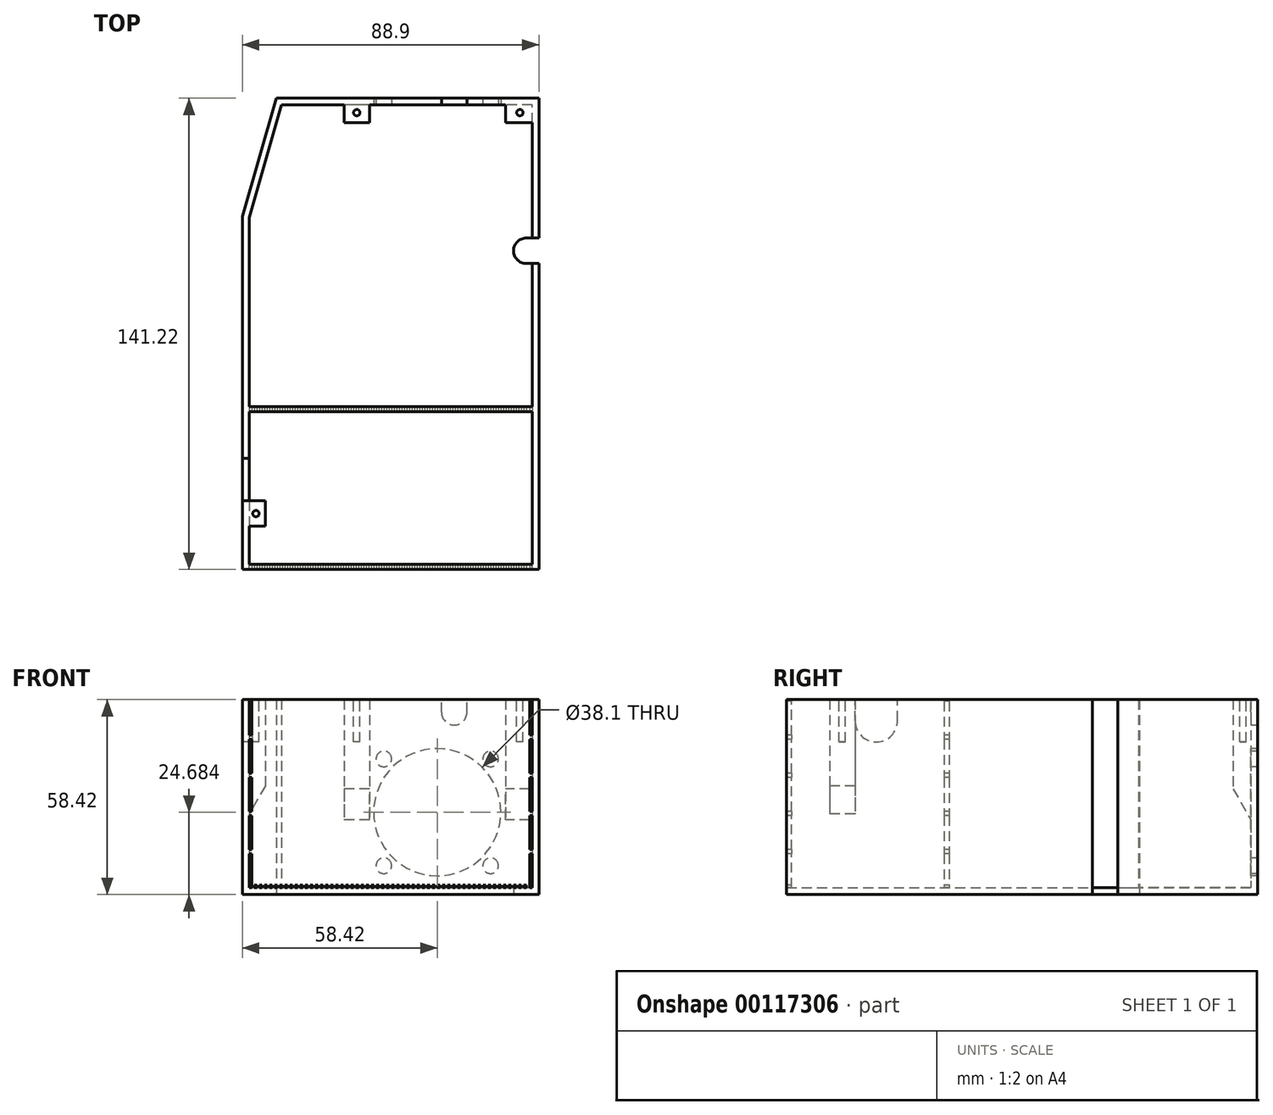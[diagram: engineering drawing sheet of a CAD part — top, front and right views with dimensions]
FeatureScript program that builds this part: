
annotation { "Feature Type Name" : "Feature", "Feature Type Description" : "" }
export const myFeature = defineFeature(function(context is Context, id is Id, definition is map)
    precondition{}
    {
        {
            var Q0;
            Q0=qCreatedBy(makeId("Top.planeOp"),FACE);
            var sketch = newSketch(context, id + "F0", { "sketchPlane" : qUnion([Q0])});
            skLineSegment(sketch, "E0.bottom", {"start": v(44.45, -69.85) * mm, "end": v(-44.45, -69.85) * mm});
            skLineSegment(sketch, "E0.top", {"start": v(44.45, 69.85) * mm, "end": v(-44.45, 69.85) * mm});
            skLineSegment(sketch, "E0.left", {"start": v(44.45, -69.85) * mm, "end": v(44.45, 69.85) * mm});
            skLineSegment(sketch, "E0.right", {"start": v(-44.45, -69.85) * mm, "end": v(-44.45, 69.85) * mm});
            skPoint(sketch, "E0.middle", {"position": v(0, 0) * mm});
            skLineSegment(sketch, "E1", {"start": v(-34.29, 69.85) * mm, "end": v(-44.45, 34.42) * mm});
            skSolve(sketch);
        }
        {
            var Q0;
            Q0=makeQuery(id+"F0.imprint","IMPRINT",FACE,{"disambiguationData":[TD([[makeQuery(id+"F0.imprint","IMPRINT",EDGE,{"derivedFrom":sQuery(id+"F0.wireOp",EDGE,"E0.bottom")}),-1.0]])]});
            extrude(context, id + "F1", {"entities" : qUnion([Q0]), "depth" : 58.42 * mm});
        }
        {
            var Q0;
            Q0=makeQuery(id+"F1.opExtrude","CAP_FACE",FACE,{"disambiguationData":[OSD([sQuery(id+"F0.wireOp",EDGE,"E0.bottom"),sQuery(id+"F0.wireOp",EDGE,"E0.top"),sQuery(id+"F0.wireOp",EDGE,"E0.left"),sQuery(id+"F0.wireOp",EDGE,"E0.right")])],"isStart":false});
            shell(context, id + "F2", {"entities" : qUnion([Q0]), "thickness" : 2.03 * mm});
        }
        {
            var Q0;
            Q0=makeQuery(id+"F2.opShell","OFFSET_FACE",FACE,{"disambiguationData":[OSD([sQuery(id+"F0.wireOp",EDGE,"E0.bottom"),sQuery(id+"F0.wireOp",EDGE,"E0.top"),sQuery(id+"F0.wireOp",EDGE,"E0.left"),sQuery(id+"F0.wireOp",EDGE,"E0.right")])]});
            var sketch = newSketch(context, id + "F3", { "sketchPlane" : qUnion([Q0])});
            skLineSegment(sketch, "E2.bottom", {"start": v(42.42, 67.82) * mm, "end": v(34.42, 67.82) * mm});
            skLineSegment(sketch, "E2.top", {"start": v(42.42, 62.48) * mm, "end": v(34.42, 62.48) * mm});
            skLineSegment(sketch, "E2.left", {"start": v(42.42, 67.82) * mm, "end": v(42.42, 62.48) * mm});
            skLineSegment(sketch, "E2.right", {"start": v(34.42, 67.82) * mm, "end": v(34.42, 62.48) * mm});
            skLineSegment(sketch, "E3.bottom", {"start": v(-13.97, 67.82) * mm, "end": v(-6.35, 67.82) * mm});
            skLineSegment(sketch, "E3.top", {"start": v(-13.97, 62.48) * mm, "end": v(-6.35, 62.48) * mm});
            skLineSegment(sketch, "E3.left", {"start": v(-13.97, 67.82) * mm, "end": v(-13.97, 62.48) * mm});
            skLineSegment(sketch, "E3.right", {"start": v(-6.35, 67.82) * mm, "end": v(-6.35, 62.48) * mm});
            skLineSegment(sketch, "E4.bottom", {"start": v(-42.42, -50.8) * mm, "end": v(-37.6, -50.8) * mm});
            skLineSegment(sketch, "E4.top", {"start": v(-42.42, -58.42) * mm, "end": v(-37.6, -58.42) * mm});
            skLineSegment(sketch, "E4.left", {"start": v(-42.42, -50.8) * mm, "end": v(-42.42, -58.42) * mm});
            skLineSegment(sketch, "E4.right", {"start": v(-37.6, -50.8) * mm, "end": v(-37.6, -58.42) * mm});
            skLineSegment(sketch, "E5.bottom", {"start": v(-42.42, -22.6) * mm, "end": v(42.42, -22.6) * mm});
            skLineSegment(sketch, "E5.top", {"start": v(-42.42, -24.13) * mm, "end": v(42.42, -24.13) * mm});
            skLineSegment(sketch, "E5.left", {"start": v(-42.42, -22.6) * mm, "end": v(-42.42, -24.13) * mm});
            skLineSegment(sketch, "E5.right", {"start": v(42.42, -22.6) * mm, "end": v(42.42, -24.13) * mm});
            skSolve(sketch);
        }
        {
            var Q0;
            Q0 = qSketchRegion(id + "F3", true);
            extrude(context, id + "F4", {"entities" : qUnion([Q0]), "operationType" : NewBodyOperationType.ADD, "depth" : 56.4 * mm});
        }
        {
            var Q0;
            Q0=makeQuery(id+"F4.boolean.opBoolean","MERGE",FACE,{"derivedFrom":[makeQuery(id+"F1.opExtrude","CAP_FACE",FACE,{"disambiguationData":[OSD([sQuery(id+"F0.wireOp",EDGE,"E0.bottom"),sQuery(id+"F0.wireOp",EDGE,"E0.top"),sQuery(id+"F0.wireOp",EDGE,"E0.left"),sQuery(id+"F0.wireOp",EDGE,"E0.right")])],"isStart":false}),makeQuery(id+"F4.opExtrude","CAP_FACE",FACE,{"disambiguationData":[OSD([sQuery(id+"F3.wireOp",EDGE,"E2.bottom"),sQuery(id+"F3.wireOp",EDGE,"E2.top"),sQuery(id+"F3.wireOp",EDGE,"E2.left"),sQuery(id+"F3.wireOp",EDGE,"E2.right")])],"isStart":false}),makeQuery(id+"F4.opExtrude","CAP_FACE",FACE,{"disambiguationData":[OSD([sQuery(id+"F3.wireOp",EDGE,"E3.bottom"),sQuery(id+"F3.wireOp",EDGE,"E3.top"),sQuery(id+"F3.wireOp",EDGE,"E3.left"),sQuery(id+"F3.wireOp",EDGE,"E3.right")])],"isStart":false}),makeQuery(id+"F4.opExtrude","CAP_FACE",FACE,{"disambiguationData":[OSD([sQuery(id+"F3.wireOp",EDGE,"E4.bottom"),sQuery(id+"F3.wireOp",EDGE,"E4.top"),sQuery(id+"F3.wireOp",EDGE,"E4.left"),sQuery(id+"F3.wireOp",EDGE,"E4.right")])],"isStart":false})]});
            var sketch = newSketch(context, id + "F5", { "sketchPlane" : qUnion([Q0])});
            skCircle(sketch, "E6", {"center": v(38.74, 65.53) * mm, "radius": 0.95 * mm});
            skCircle(sketch, "E7", {"center": v(-10.16, 65.53) * mm, "radius": 0.95 * mm});
            skCircle(sketch, "E8", {"center": v(-40.39, -54.6) * mm, "radius": 0.95 * mm});
            skSolve(sketch);
        }
        {
            var Q0;
            Q0 = qSketchRegion(id + "F5", true);
            extrude(context, id + "F6", {"entities" : qUnion([Q0]), "operationType" : NewBodyOperationType.REMOVE, "oppositeDirection" : true, "depth" : 12.7 * mm});
        }
        {
            var Q0;
            Q0=makeQuery(id+"F2.opShell","OFFSET_FACE",FACE,{"disambiguationData":[OSD([sQuery(id+"F0.wireOp",EDGE,"E0.bottom")])]});
            extrude(context, id + "F7", {"entities" : qUnion([Q0]), "operationType" : NewBodyOperationType.REMOVE, "endBound" : BoundingType.UP_TO_NEXT, "oppositeDirection" : true, "depth" : 25.4 * mm});
        }
        {
            var Q0;
            Q0=makeQuery(id+"F1.opExtrude","SWEPT_FACE",FACE,{"disambiguationData":[OSD([sQuery(id+"F0.wireOp",EDGE,"E0.top")])]});
            var sketch = newSketch(context, id + "F8", { "sketchPlane" : qUnion([Q0])});
            skArc(sketch, "E9", {"start": v(-22.86, 54.6) * mm, "mid": v(-19.05, 50.8) * mm, "end": v(-15.24, 54.6) * mm});
            skLineSegment(sketch, "E10", {"start": v(-15.24, 54.6) * mm, "end": v(-15.24, 58.42) * mm});
            skLineSegment(sketch, "E11", {"start": v(-22.86, 54.6) * mm, "end": v(-22.86, 58.42) * mm});
            skLineSegment(sketch, "E12", {"start": v(-15.24, 58.42) * mm, "end": v(-22.86, 58.42) * mm});
            skSolve(sketch);
        }
        {
            var Q0;
            Q0 = qSketchRegion(id + "F8", true);
            extrude(context, id + "F9", {"entities" : qUnion([Q0]), "operationType" : NewBodyOperationType.REMOVE, "endBound" : BoundingType.UP_TO_NEXT, "oppositeDirection" : true, "depth" : 25.4 * mm});
        }
        {
            var Q0;
            Q0=makeQuery(id+"F1.opExtrude","SWEPT_FACE",FACE,{"disambiguationData":[OSD([sQuery(id+"F0.wireOp",EDGE,"E0.left")])]});
            var sketch = newSketch(context, id + "F10", { "sketchPlane" : qUnion([Q0])});
            skLineSegment(sketch, "E13", {"start": v(27.94, 6.35) * mm, "end": v(27.94, 58.42) * mm});
            skLineSegment(sketch, "E14", {"start": v(20.32, 6.35) * mm, "end": v(20.32, 58.42) * mm});
            skLineSegment(sketch, "E15", {"start": v(20.32, 58.42) * mm, "end": v(27.94, 58.42) * mm});
            skLineSegment(sketch, "E16", {"start": v(20.32, 6.35) * mm, "end": v(20.32, 2.54) * mm});
            skLineSegment(sketch, "E17", {"start": v(20.32, 2.54) * mm, "end": v(27.94, 2.54) * mm});
            skLineSegment(sketch, "E18", {"start": v(27.94, 2.54) * mm, "end": v(27.94, 6.35) * mm});
            skSolve(sketch);
        }
        {
            var Q0;
            Q0 = qSketchRegion(id + "F10", true);
            extrude(context, id + "F11", {"entities" : qUnion([Q0]), "operationType" : NewBodyOperationType.REMOVE, "endBound" : BoundingType.UP_TO_NEXT, "oppositeDirection" : true, "depth" : 25.4 * mm});
        }
        {
            var Q0;
            Q0=makeQuery(id+"F1.opExtrude","SWEPT_FACE",FACE,{"disambiguationData":[OSD([sQuery(id+"F0.wireOp",EDGE,"E0.right")])]});
            var sketch = newSketch(context, id + "F12", { "sketchPlane" : qUnion([Q0])});
            skArc(sketch, "E19", {"start": v(38.1, 52.07) * mm, "mid": v(44.45, 45.72) * mm, "end": v(50.8, 52.07) * mm});
            skLineSegment(sketch, "E20", {"start": v(50.8, 52.07) * mm, "end": v(50.8, 58.42) * mm});
            skLineSegment(sketch, "E21", {"start": v(38.1, 52.07) * mm, "end": v(38.1, 58.42) * mm});
            skLineSegment(sketch, "E22", {"start": v(38.1, 58.42) * mm, "end": v(50.8, 58.42) * mm});
            skSolve(sketch);
        }
        {
            var Q0;
            Q0 = qSketchRegion(id + "F12", true);
            extrude(context, id + "F13", {"entities" : qUnion([Q0]), "operationType" : NewBodyOperationType.REMOVE, "endBound" : BoundingType.UP_TO_NEXT, "oppositeDirection" : true, "depth" : 25.4 * mm});
        }
        {
            var Q0;
            Q0=makeQuery(id+"F1.opExtrude","CAP_FACE",FACE,{"disambiguationData":[OSD([sQuery(id+"F0.wireOp",EDGE,"E0.bottom"),sQuery(id+"F0.wireOp",EDGE,"E0.top"),sQuery(id+"F0.wireOp",EDGE,"E0.left"),sQuery(id+"F0.wireOp",EDGE,"E0.right")])],"isStart":true});
            var sketch = newSketch(context, id + "F14", { "sketchPlane" : qUnion([Q0])});
            skLineSegment(sketch, "E23", {"start": v(-34.29, -69.85) * mm, "end": v(-44.45, -34.42) * mm});
            skSolve(sketch);
        }
        {
            var Q0;
            Q0=makeQuery(id+"F4.opExtrude","SWEPT_FACE",FACE,{"disambiguationData":[OSD([sQuery(id+"F3.wireOp",EDGE,"E4.top")])]});
            var sketch = newSketch(context, id + "F15", { "sketchPlane" : qUnion([Q0])});
            skLineSegment(sketch, "E24", {"start": v(-37.6, 32.58) * mm, "end": v(-42.42, 24.22) * mm});
            skLineSegment(sketch, "E25", {"start": v(-42.42, 24.22) * mm, "end": v(-42.42, 2.03) * mm});
            skLineSegment(sketch, "E26", {"start": v(-42.42, 2.03) * mm, "end": v(-37.6, 2.03) * mm});
            skLineSegment(sketch, "E27", {"start": v(-37.6, 2.03) * mm, "end": v(-37.6, 32.58) * mm});
            skSolve(sketch);
        }
        {
            var Q0;
            Q0 = qSketchRegion(id + "F15", true);
            extrude(context, id + "F16", {"entities" : qUnion([Q0]), "operationType" : NewBodyOperationType.REMOVE, "endBound" : BoundingType.UP_TO_NEXT, "oppositeDirection" : true, "depth" : 25.4 * mm});
        }
        {
            var Q0;
            Q0=makeQuery(id+"F4.opExtrude","SWEPT_FACE",FACE,{"disambiguationData":[OSD([sQuery(id+"F3.wireOp",EDGE,"E3.left")])]});
            var sketch = newSketch(context, id + "F17", { "sketchPlane" : qUnion([Q0])});
            skLineSegment(sketch, "E28", {"start": v(-62.48, 31.7) * mm, "end": v(-67.82, 22.46) * mm});
            skSolve(sketch);
        }
        {
            var Q0;
            {var subQ0=sQuery(id+"F17.wireOp",EDGE,"E28");Q0=makeQuery(id+"F17.imprint","IMPRINT",FACE,{"disambiguationData":[TD([[makeQuery(id+"F17.imprint","IMPRINT",EDGE,{"derivedFrom":subQ0}),1.0]])]});}
            extrude(context, id + "F18", {"entities" : qUnion([Q0]), "operationType" : NewBodyOperationType.REMOVE, "oppositeDirection" : true, "depth" : 56.4 * mm});
        }
        {
            var Q0;
            {var subQ0=sQuery(id+"F3.wireOp",EDGE,"E3.left");var subQ1=sQuery(id+"F3.wireOp",EDGE,"E3.bottom");var subQ2=sQuery(id+"F0.wireOp",EDGE,"E0.top");var subQ3=sQuery(id+"F3.wireOp",EDGE,"E2.right");var subQ6=sQuery(id+"F0.wireOp",EDGE,"E1");var subQ14=makeQuery(id+"F2.opShell","OFFSET_FACE",FACE,{"disambiguationData":[OSD([subQ2])]});Q0=makeQuery(id+"F18.boolean.opBoolean","MERGE",FACE,{"derivedFrom":[makeQuery(id+"F4.boolean.opBoolean","SPLIT",FACE,{"disambiguationData":[TD([makeQuery(id+"F2.opShell","OFFSET_FACE",FACE,{"disambiguationData":[OSD([subQ6])]})])],"derivedFrom":subQ14}),makeQuery(id+"F4.boolean.opBoolean","SPLIT",FACE,{"disambiguationData":[TD([makeQuery(id+"F4.opExtrude","SWEPT_FACE",FACE,{"disambiguationData":[OSD([subQ3])]})])],"derivedFrom":subQ14}),makeQuery(id+"F18.opExtrude","SWEPT_FACE",FACE,{"disambiguationData":[OSD([subQ2,subQ1,subQ0])]})]});}
            var sketch = newSketch(context, id + "F19", { "sketchPlane" : qUnion([Q0])});
            skCircle(sketch, "E29", {"center": v(-2.03, 8.64) * mm, "radius": 2.35 * mm});
            skCircle(sketch, "E30", {"center": v(29.97, 8.64) * mm, "radius": 2.35 * mm});
            skCircle(sketch, "E31", {"center": v(-2.03, 40.64) * mm, "radius": 2.35 * mm});
            skCircle(sketch, "E32", {"center": v(29.97, 40.64) * mm, "radius": 2.35 * mm});
            skCircle(sketch, "E33", {"center": v(13.97, 24.68) * mm, "radius": 19.05 * mm});
            skSolve(sketch);
        }
        {
            var Q0;
            Q0 = qSketchRegion(id + "F19", true);
            extrude(context, id + "F20", {"entities" : qUnion([Q0]), "operationType" : NewBodyOperationType.REMOVE, "endBound" : BoundingType.UP_TO_NEXT, "oppositeDirection" : true, "depth" : 25.4 * mm});
        }
        {
            var Q0;
            Q0=makeQuery(id+"F14.imprint","IMPRINT",FACE,{"disambiguationData":[TD([[makeQuery(id+"F14.imprint","IMPRINT",EDGE,{"derivedFrom":sQuery(id+"F14.wireOp",EDGE,"E23")}),-1.0]])]});
            var sketch = newSketch(context, id + "F21", { "sketchPlane" : qUnion([Q0])});
            skCircle(sketch, "E34", {"center": v(-8.9, -19.05) * mm, "radius": 19.05 * mm});
            skCircle(sketch, "E35", {"center": v(6.99, -35) * mm, "radius": 2.35 * mm});
            skCircle(sketch, "E36", {"center": v(-25.02, -35) * mm, "radius": 2.35 * mm});
            skCircle(sketch, "E37", {"center": v(-25.02, -3) * mm, "radius": 2.35 * mm});
            skCircle(sketch, "E38", {"center": v(6.99, -3) * mm, "radius": 2.35 * mm});
            skCircle(sketch, "E39", {"center": v(-25.02, -35) * mm, "radius": 1.52 * mm});
            skCircle(sketch, "E40", {"center": v(6.99, -35) * mm, "radius": 1.52 * mm});
            skCircle(sketch, "E41", {"center": v(6.99, -3) * mm, "radius": 1.52 * mm});
            skCircle(sketch, "E42", {"center": v(-25.02, -3) * mm, "radius": 1.52 * mm});
            skCircle(sketch, "E43", {"center": v(-8.9, -19.05) * mm, "radius": 17.78 * mm});
            skLineSegment(sketch, "E44", {"start": v(-8.9, -44.54) * mm, "end": v(-8.9, 4.8) * mm, "construction": true});
            skLineSegment(sketch, "E45", {"start": v(-33.52, -19.05) * mm, "end": v(14.85, -19.05) * mm, "construction": true});
            skLineSegment(sketch, "E46", {"start": v(-9.98, -36.8) * mm, "end": v(-10.05, -38.06) * mm});
            skLineSegment(sketch, "E47.MirrorCS", {"start": v(-7.8, -36.8) * mm, "end": v(-7.73, -38.06) * mm});
            skLineSegment(sketch, "E48", {"start": v(8.86, -20.14) * mm, "end": v(10.12, -20.21) * mm});
            skLineSegment(sketch, "E49.MirrorCS", {"start": v(8.86, -17.96) * mm, "end": v(10.12, -17.89) * mm});
            skLineSegment(sketch, "E50", {"start": v(-8.2, -1.28) * mm, "end": v(-8.11, -0.02) * mm});
            skLineSegment(sketch, "E51", {"start": v(-26.64, -17.95) * mm, "end": v(-27.9, -17.87) * mm});
            skLineSegment(sketch, "E52.MirrorCS", {"start": v(-9.59, -1.28) * mm, "end": v(-9.67, -0.02) * mm});
            skLineSegment(sketch, "E53", {"start": v(-27.9, -20.23) * mm, "end": v(-26.64, -20.15) * mm});
            skSolve(sketch);
        }
        {
            var Q0;
            Q0=makeQuery(id+"F1.opExtrude","CAP_FACE",FACE,{"disambiguationData":[OSD([sQuery(id+"F0.wireOp",EDGE,"E0.bottom"),sQuery(id+"F0.wireOp",EDGE,"E0.top"),sQuery(id+"F0.wireOp",EDGE,"E0.left"),sQuery(id+"F0.wireOp",EDGE,"E0.right"),sQuery(id+"F0.wireOp",EDGE,"E1")])],"isStart":true});
            var sketch = newSketch(context, id + "F22", { "sketchPlane" : qUnion([Q0])});
            skLineSegment(sketch, "E54", {"start": v(44.45, -27.94) * mm, "end": v(40.64, -27.94) * mm});
            skLineSegment(sketch, "E55", {"start": v(44.45, -20.32) * mm, "end": v(40.64, -20.32) * mm});
            skArc(sketch, "E56", {"start": v(40.64, -27.94) * mm, "mid": v(36.83, -24.13) * mm, "end": v(40.64, -20.32) * mm});
            skLineSegment(sketch, "E57", {"start": v(44.45, -20.32) * mm, "end": v(44.45, -27.94) * mm});
            skSolve(sketch);
        }
        {
            var Q0;
            Q0 = qSketchRegion(id + "F22", true);
            extrude(context, id + "F23", {"entities" : qUnion([Q0]), "operationType" : NewBodyOperationType.REMOVE, "endBound" : BoundingType.UP_TO_NEXT, "oppositeDirection" : true, "depth" : 25.4 * mm});
        }
        {
            var Q0;
            Q0=makeQuery(id+"F1.opExtrude","SWEPT_FACE",FACE,{"disambiguationData":[OSD([sQuery(id+"F0.wireOp",EDGE,"E0.bottom")])]});
            var sketch = newSketch(context, id + "F24", { "sketchPlane" : qUnion([Q0])});
            skLineSegment(sketch, "E58.bottom", {"start": v(-44.45, 58.42) * mm, "end": v(44.45, 58.42) * mm});
            skLineSegment(sketch, "E58.top", {"start": v(-44.45, 0) * mm, "end": v(44.45, 0) * mm});
            skLineSegment(sketch, "E58.left", {"start": v(-44.45, 58.42) * mm, "end": v(-44.45, 0) * mm});
            skLineSegment(sketch, "E58.right", {"start": v(44.45, 58.42) * mm, "end": v(44.45, 0) * mm});
            skSolve(sketch);
        }
        {
            var Q0;
            Q0 = qSketchRegion(id + "F24", true);
            extrude(context, id + "F25", {"entities" : qUnion([Q0]), "operationType" : NewBodyOperationType.ADD, "depth" : 1.52 * mm});
        }
        {
            var Q0;
            Q0=makeQuery(id+"F25.opExtrude","CAP_FACE",FACE,{"disambiguationData":[OSD([sQuery(id+"F24.wireOp",EDGE,"E58.bottom"),sQuery(id+"F24.wireOp",EDGE,"E58.top"),sQuery(id+"F24.wireOp",EDGE,"E58.left"),sQuery(id+"F24.wireOp",EDGE,"E58.right")])],"isStart":false});
            var sketch = newSketch(context, id + "F26", { "sketchPlane" : qUnion([Q0])});
            skLineSegment(sketch, "E59.bottom", {"start": v(-42.42, 12.2) * mm, "end": v(-41.66, 12.2) * mm});
            skLineSegment(sketch, "E59.top", {"start": v(-42.42, 2.03) * mm, "end": v(-41.66, 2.03) * mm});
            skLineSegment(sketch, "E59.left", {"start": v(-42.42, 12.2) * mm, "end": v(-42.42, 2.03) * mm});
            skLineSegment(sketch, "E59.right", {"start": v(-41.66, 12.2) * mm, "end": v(-41.66, 2.03) * mm});
            skLineSegment(sketch, "E60.0.1.0", {"start": v(-42.42, 23.62) * mm, "end": v(-42.42, 13.46) * mm});
            skLineSegment(sketch, "E60.0.1.1", {"start": v(-41.66, 23.62) * mm, "end": v(-41.66, 13.46) * mm});
            skLineSegment(sketch, "E60.0.1.2", {"start": v(-42.42, 23.62) * mm, "end": v(-41.66, 23.62) * mm});
            skLineSegment(sketch, "E60.0.1.3", {"start": v(-42.42, 13.46) * mm, "end": v(-41.66, 13.46) * mm});
            skLineSegment(sketch, "E60.0.2.0", {"start": v(-42.42, 35.05) * mm, "end": v(-42.42, 24.9) * mm});
            skLineSegment(sketch, "E60.0.2.1", {"start": v(-41.66, 35.05) * mm, "end": v(-41.66, 24.9) * mm});
            skLineSegment(sketch, "E60.0.2.2", {"start": v(-42.42, 35.05) * mm, "end": v(-41.66, 35.05) * mm});
            skLineSegment(sketch, "E60.0.2.3", {"start": v(-42.42, 24.9) * mm, "end": v(-41.66, 24.9) * mm});
            skLineSegment(sketch, "E60.0.3.0", {"start": v(-42.42, 46.48) * mm, "end": v(-42.42, 36.32) * mm});
            skLineSegment(sketch, "E60.0.3.1", {"start": v(-41.66, 46.48) * mm, "end": v(-41.66, 36.32) * mm});
            skLineSegment(sketch, "E60.0.3.2", {"start": v(-42.42, 46.48) * mm, "end": v(-41.66, 46.48) * mm});
            skLineSegment(sketch, "E60.0.3.3", {"start": v(-42.42, 36.32) * mm, "end": v(-41.66, 36.32) * mm});
            skLineSegment(sketch, "E60.0.4.0", {"start": v(-42.42, 57.91) * mm, "end": v(-42.42, 47.75) * mm});
            skLineSegment(sketch, "E60.0.4.1", {"start": v(-41.66, 57.91) * mm, "end": v(-41.66, 47.75) * mm});
            skLineSegment(sketch, "E60.0.4.2", {"start": v(-42.42, 57.91) * mm, "end": v(-41.66, 57.91) * mm});
            skLineSegment(sketch, "E60.0.4.3", {"start": v(-42.42, 47.75) * mm, "end": v(-41.66, 47.75) * mm});
            skLineSegment(sketch, "E60.direction1", {"start": v(-42.42, 2.03) * mm, "end": v(-36.73, 2.03) * mm, "construction": true});
            skLineSegment(sketch, "E60.direction2", {"start": v(-42.42, 2.03) * mm, "end": v(-42.42, 13.46) * mm, "construction": true});
            skLineSegment(sketch, "E61.1.0.0", {"start": v(42.42, 35.05) * mm, "end": v(42.42, 24.9) * mm});
            skLineSegment(sketch, "E61.1.0.1", {"start": v(41.66, 35.05) * mm, "end": v(41.66, 24.9) * mm});
            skLineSegment(sketch, "E61.1.0.3", {"start": v(41.66, 57.91) * mm, "end": v(41.66, 47.75) * mm});
            skLineSegment(sketch, "E61.1.0.12", {"start": v(41.66, 23.62) * mm, "end": v(41.66, 13.46) * mm});
            skLineSegment(sketch, "E61.1.0.19", {"start": v(42.42, 12.2) * mm, "end": v(42.42, 2.03) * mm});
            skLineSegment(sketch, "E61.1.0.20", {"start": v(41.66, 46.48) * mm, "end": v(41.66, 36.32) * mm});
            skLineSegment(sketch, "E61.1.0.21", {"start": v(42.42, 46.48) * mm, "end": v(42.42, 36.32) * mm});
            skLineSegment(sketch, "E61.1.0.22", {"start": v(41.66, 2.03) * mm, "end": v(41.66, 13.46) * mm, "construction": true});
            skLineSegment(sketch, "E61.1.0.26", {"start": v(41.66, 2.03) * mm, "end": v(47.34, 2.03) * mm, "construction": true});
            skLineSegment(sketch, "E61.1.0.29", {"start": v(42.42, 57.91) * mm, "end": v(42.42, 47.75) * mm});
            skLineSegment(sketch, "E61.1.0.30", {"start": v(42.42, 23.62) * mm, "end": v(42.42, 13.46) * mm});
            skLineSegment(sketch, "E61.1.0.31", {"start": v(41.66, 12.2) * mm, "end": v(41.66, 2.03) * mm});
            skLineSegment(sketch, "E61.1.0.32", {"start": v(41.66, 13.46) * mm, "end": v(42.42, 13.46) * mm});
            skLineSegment(sketch, "E61.1.0.33", {"start": v(41.66, 23.62) * mm, "end": v(42.42, 23.62) * mm});
            skLineSegment(sketch, "E61.1.0.50", {"start": v(41.66, 57.91) * mm, "end": v(42.42, 57.91) * mm});
            skLineSegment(sketch, "E61.1.0.53", {"start": v(41.66, 2.03) * mm, "end": v(42.42, 2.03) * mm});
            skLineSegment(sketch, "E61.1.0.54", {"start": v(41.66, 12.2) * mm, "end": v(42.42, 12.2) * mm});
            skLineSegment(sketch, "E61.1.0.55", {"start": v(41.66, 36.32) * mm, "end": v(42.42, 36.32) * mm});
            skLineSegment(sketch, "E61.1.0.56", {"start": v(41.66, 47.75) * mm, "end": v(42.42, 47.75) * mm});
            skLineSegment(sketch, "E61.1.0.59", {"start": v(41.66, 24.9) * mm, "end": v(42.42, 24.9) * mm});
            skLineSegment(sketch, "E61.1.0.60", {"start": v(41.66, 35.05) * mm, "end": v(42.42, 35.05) * mm});
            skLineSegment(sketch, "E61.1.0.61", {"start": v(41.66, 46.48) * mm, "end": v(42.42, 46.48) * mm});
            skLineSegment(sketch, "E61.direction1", {"start": v(-42.42, 2.03) * mm, "end": v(41.66, 2.03) * mm, "construction": true});
            skLineSegment(sketch, "E62.bottom", {"start": v(-40.9, 2.8) * mm, "end": v(-40.13, 2.8) * mm});
            skLineSegment(sketch, "E62.top", {"start": v(-40.9, 2.03) * mm, "end": v(-40.13, 2.03) * mm});
            skLineSegment(sketch, "E62.left", {"start": v(-40.9, 2.8) * mm, "end": v(-40.9, 2.03) * mm});
            skLineSegment(sketch, "E62.right", {"start": v(-40.13, 2.8) * mm, "end": v(-40.13, 2.03) * mm});
            skLineSegment(sketch, "E63.1.0.0", {"start": v(-39.37, 2.8) * mm, "end": v(-38.6, 2.8) * mm});
            skLineSegment(sketch, "E63.1.0.1", {"start": v(-38.6, 2.8) * mm, "end": v(-38.6, 2.03) * mm});
            skLineSegment(sketch, "E63.1.0.2", {"start": v(-39.37, 2.8) * mm, "end": v(-39.37, 2.03) * mm});
            skLineSegment(sketch, "E63.1.0.3", {"start": v(-39.37, 2.03) * mm, "end": v(-38.6, 2.03) * mm});
            skLineSegment(sketch, "E63.2.0.0", {"start": v(-37.85, 2.8) * mm, "end": v(-37.08, 2.8) * mm});
            skLineSegment(sketch, "E63.2.0.1", {"start": v(-37.08, 2.8) * mm, "end": v(-37.08, 2.03) * mm});
            skLineSegment(sketch, "E63.2.0.2", {"start": v(-37.85, 2.8) * mm, "end": v(-37.85, 2.03) * mm});
            skLineSegment(sketch, "E63.2.0.3", {"start": v(-37.85, 2.03) * mm, "end": v(-37.08, 2.03) * mm});
            skLineSegment(sketch, "E63.3.0.0", {"start": v(-36.32, 2.8) * mm, "end": v(-35.56, 2.8) * mm});
            skLineSegment(sketch, "E63.3.0.1", {"start": v(-35.56, 2.8) * mm, "end": v(-35.56, 2.03) * mm});
            skLineSegment(sketch, "E63.3.0.2", {"start": v(-36.32, 2.8) * mm, "end": v(-36.32, 2.03) * mm});
            skLineSegment(sketch, "E63.3.0.3", {"start": v(-36.32, 2.03) * mm, "end": v(-35.56, 2.03) * mm});
            skLineSegment(sketch, "E63.4.0.0", {"start": v(-34.8, 2.8) * mm, "end": v(-34.04, 2.8) * mm});
            skLineSegment(sketch, "E63.4.0.1", {"start": v(-34.04, 2.8) * mm, "end": v(-34.04, 2.03) * mm});
            skLineSegment(sketch, "E63.4.0.2", {"start": v(-34.8, 2.8) * mm, "end": v(-34.8, 2.03) * mm});
            skLineSegment(sketch, "E63.4.0.3", {"start": v(-34.8, 2.03) * mm, "end": v(-34.04, 2.03) * mm});
            skLineSegment(sketch, "E63.5.0.0", {"start": v(-33.27, 2.8) * mm, "end": v(-32.51, 2.8) * mm});
            skLineSegment(sketch, "E63.5.0.1", {"start": v(-32.51, 2.8) * mm, "end": v(-32.51, 2.03) * mm});
            skLineSegment(sketch, "E63.5.0.2", {"start": v(-33.27, 2.8) * mm, "end": v(-33.27, 2.03) * mm});
            skLineSegment(sketch, "E63.5.0.3", {"start": v(-33.27, 2.03) * mm, "end": v(-32.51, 2.03) * mm});
            skLineSegment(sketch, "E63.6.0.0", {"start": v(-31.75, 2.8) * mm, "end": v(-30.99, 2.8) * mm});
            skLineSegment(sketch, "E63.6.0.1", {"start": v(-30.99, 2.8) * mm, "end": v(-30.99, 2.03) * mm});
            skLineSegment(sketch, "E63.6.0.2", {"start": v(-31.75, 2.8) * mm, "end": v(-31.75, 2.03) * mm});
            skLineSegment(sketch, "E63.6.0.3", {"start": v(-31.75, 2.03) * mm, "end": v(-30.99, 2.03) * mm});
            skLineSegment(sketch, "E63.7.0.0", {"start": v(-30.23, 2.8) * mm, "end": v(-29.46, 2.8) * mm});
            skLineSegment(sketch, "E63.7.0.1", {"start": v(-29.46, 2.8) * mm, "end": v(-29.46, 2.03) * mm});
            skLineSegment(sketch, "E63.7.0.2", {"start": v(-30.23, 2.8) * mm, "end": v(-30.23, 2.03) * mm});
            skLineSegment(sketch, "E63.7.0.3", {"start": v(-30.23, 2.03) * mm, "end": v(-29.46, 2.03) * mm});
            skLineSegment(sketch, "E63.8.0.0", {"start": v(-28.7, 2.8) * mm, "end": v(-27.94, 2.8) * mm});
            skLineSegment(sketch, "E63.8.0.1", {"start": v(-27.94, 2.8) * mm, "end": v(-27.94, 2.03) * mm});
            skLineSegment(sketch, "E63.8.0.2", {"start": v(-28.7, 2.8) * mm, "end": v(-28.7, 2.03) * mm});
            skLineSegment(sketch, "E63.8.0.3", {"start": v(-28.7, 2.03) * mm, "end": v(-27.94, 2.03) * mm});
            skLineSegment(sketch, "E63.9.0.0", {"start": v(-27.18, 2.8) * mm, "end": v(-26.42, 2.8) * mm});
            skLineSegment(sketch, "E63.9.0.1", {"start": v(-26.42, 2.8) * mm, "end": v(-26.42, 2.03) * mm});
            skLineSegment(sketch, "E63.9.0.2", {"start": v(-27.18, 2.8) * mm, "end": v(-27.18, 2.03) * mm});
            skLineSegment(sketch, "E63.9.0.3", {"start": v(-27.18, 2.03) * mm, "end": v(-26.42, 2.03) * mm});
            skLineSegment(sketch, "E63.10.0.0", {"start": v(-25.65, 2.8) * mm, "end": v(-24.9, 2.8) * mm});
            skLineSegment(sketch, "E63.10.0.1", {"start": v(-24.9, 2.8) * mm, "end": v(-24.9, 2.03) * mm});
            skLineSegment(sketch, "E63.10.0.2", {"start": v(-25.65, 2.8) * mm, "end": v(-25.65, 2.03) * mm});
            skLineSegment(sketch, "E63.10.0.3", {"start": v(-25.65, 2.03) * mm, "end": v(-24.9, 2.03) * mm});
            skLineSegment(sketch, "E63.11.0.0", {"start": v(-24.13, 2.8) * mm, "end": v(-23.37, 2.8) * mm});
            skLineSegment(sketch, "E63.11.0.1", {"start": v(-23.37, 2.8) * mm, "end": v(-23.37, 2.03) * mm});
            skLineSegment(sketch, "E63.11.0.2", {"start": v(-24.13, 2.8) * mm, "end": v(-24.13, 2.03) * mm});
            skLineSegment(sketch, "E63.11.0.3", {"start": v(-24.13, 2.03) * mm, "end": v(-23.37, 2.03) * mm});
            skLineSegment(sketch, "E63.12.0.0", {"start": v(-22.6, 2.8) * mm, "end": v(-21.84, 2.8) * mm});
            skLineSegment(sketch, "E63.12.0.1", {"start": v(-21.84, 2.8) * mm, "end": v(-21.84, 2.03) * mm});
            skLineSegment(sketch, "E63.12.0.2", {"start": v(-22.6, 2.8) * mm, "end": v(-22.6, 2.03) * mm});
            skLineSegment(sketch, "E63.12.0.3", {"start": v(-22.6, 2.03) * mm, "end": v(-21.84, 2.03) * mm});
            skLineSegment(sketch, "E63.13.0.0", {"start": v(-21.08, 2.8) * mm, "end": v(-20.32, 2.8) * mm});
            skLineSegment(sketch, "E63.13.0.1", {"start": v(-20.32, 2.8) * mm, "end": v(-20.32, 2.03) * mm});
            skLineSegment(sketch, "E63.13.0.2", {"start": v(-21.08, 2.8) * mm, "end": v(-21.08, 2.03) * mm});
            skLineSegment(sketch, "E63.13.0.3", {"start": v(-21.08, 2.03) * mm, "end": v(-20.32, 2.03) * mm});
            skLineSegment(sketch, "E63.14.0.0", {"start": v(-19.56, 2.8) * mm, "end": v(-18.8, 2.8) * mm});
            skLineSegment(sketch, "E63.14.0.1", {"start": v(-18.8, 2.8) * mm, "end": v(-18.8, 2.03) * mm});
            skLineSegment(sketch, "E63.14.0.2", {"start": v(-19.56, 2.8) * mm, "end": v(-19.56, 2.03) * mm});
            skLineSegment(sketch, "E63.14.0.3", {"start": v(-19.56, 2.03) * mm, "end": v(-18.8, 2.03) * mm});
            skLineSegment(sketch, "E63.15.0.0", {"start": v(-18.03, 2.8) * mm, "end": v(-17.27, 2.8) * mm});
            skLineSegment(sketch, "E63.15.0.1", {"start": v(-17.27, 2.8) * mm, "end": v(-17.27, 2.03) * mm});
            skLineSegment(sketch, "E63.15.0.2", {"start": v(-18.03, 2.8) * mm, "end": v(-18.03, 2.03) * mm});
            skLineSegment(sketch, "E63.15.0.3", {"start": v(-18.03, 2.03) * mm, "end": v(-17.27, 2.03) * mm});
            skLineSegment(sketch, "E63.16.0.0", {"start": v(-16.51, 2.8) * mm, "end": v(-15.75, 2.8) * mm});
            skLineSegment(sketch, "E63.16.0.1", {"start": v(-15.75, 2.8) * mm, "end": v(-15.75, 2.03) * mm});
            skLineSegment(sketch, "E63.16.0.2", {"start": v(-16.51, 2.8) * mm, "end": v(-16.51, 2.03) * mm});
            skLineSegment(sketch, "E63.16.0.3", {"start": v(-16.51, 2.03) * mm, "end": v(-15.75, 2.03) * mm});
            skLineSegment(sketch, "E63.17.0.0", {"start": v(-14.99, 2.8) * mm, "end": v(-14.22, 2.8) * mm});
            skLineSegment(sketch, "E63.17.0.1", {"start": v(-14.22, 2.8) * mm, "end": v(-14.22, 2.03) * mm});
            skLineSegment(sketch, "E63.17.0.2", {"start": v(-14.99, 2.8) * mm, "end": v(-14.99, 2.03) * mm});
            skLineSegment(sketch, "E63.17.0.3", {"start": v(-14.99, 2.03) * mm, "end": v(-14.22, 2.03) * mm});
            skLineSegment(sketch, "E63.18.0.0", {"start": v(-13.46, 2.8) * mm, "end": v(-12.7, 2.8) * mm});
            skLineSegment(sketch, "E63.18.0.1", {"start": v(-12.7, 2.8) * mm, "end": v(-12.7, 2.03) * mm});
            skLineSegment(sketch, "E63.18.0.2", {"start": v(-13.46, 2.8) * mm, "end": v(-13.46, 2.03) * mm});
            skLineSegment(sketch, "E63.18.0.3", {"start": v(-13.46, 2.03) * mm, "end": v(-12.7, 2.03) * mm});
            skLineSegment(sketch, "E63.19.0.0", {"start": v(-11.94, 2.8) * mm, "end": v(-11.18, 2.8) * mm});
            skLineSegment(sketch, "E63.19.0.1", {"start": v(-11.18, 2.8) * mm, "end": v(-11.18, 2.03) * mm});
            skLineSegment(sketch, "E63.19.0.2", {"start": v(-11.94, 2.8) * mm, "end": v(-11.94, 2.03) * mm});
            skLineSegment(sketch, "E63.19.0.3", {"start": v(-11.94, 2.03) * mm, "end": v(-11.18, 2.03) * mm});
            skLineSegment(sketch, "E63.20.0.0", {"start": v(-10.41, 2.8) * mm, "end": v(-9.65, 2.8) * mm});
            skLineSegment(sketch, "E63.20.0.1", {"start": v(-9.65, 2.8) * mm, "end": v(-9.65, 2.03) * mm});
            skLineSegment(sketch, "E63.20.0.2", {"start": v(-10.41, 2.8) * mm, "end": v(-10.41, 2.03) * mm});
            skLineSegment(sketch, "E63.20.0.3", {"start": v(-10.41, 2.03) * mm, "end": v(-9.65, 2.03) * mm});
            skLineSegment(sketch, "E63.21.0.0", {"start": v(-8.9, 2.8) * mm, "end": v(-8.13, 2.8) * mm});
            skLineSegment(sketch, "E63.21.0.1", {"start": v(-8.13, 2.8) * mm, "end": v(-8.13, 2.03) * mm});
            skLineSegment(sketch, "E63.21.0.2", {"start": v(-8.9, 2.8) * mm, "end": v(-8.9, 2.03) * mm});
            skLineSegment(sketch, "E63.21.0.3", {"start": v(-8.9, 2.03) * mm, "end": v(-8.13, 2.03) * mm});
            skLineSegment(sketch, "E63.22.0.0", {"start": v(-7.37, 2.8) * mm, "end": v(-6.6, 2.8) * mm});
            skLineSegment(sketch, "E63.22.0.1", {"start": v(-6.6, 2.8) * mm, "end": v(-6.6, 2.03) * mm});
            skLineSegment(sketch, "E63.22.0.2", {"start": v(-7.37, 2.8) * mm, "end": v(-7.37, 2.03) * mm});
            skLineSegment(sketch, "E63.22.0.3", {"start": v(-7.37, 2.03) * mm, "end": v(-6.6, 2.03) * mm});
            skLineSegment(sketch, "E63.23.0.0", {"start": v(-5.84, 2.8) * mm, "end": v(-5.08, 2.8) * mm});
            skLineSegment(sketch, "E63.23.0.1", {"start": v(-5.08, 2.8) * mm, "end": v(-5.08, 2.03) * mm});
            skLineSegment(sketch, "E63.23.0.2", {"start": v(-5.84, 2.8) * mm, "end": v(-5.84, 2.03) * mm});
            skLineSegment(sketch, "E63.23.0.3", {"start": v(-5.84, 2.03) * mm, "end": v(-5.08, 2.03) * mm});
            skLineSegment(sketch, "E63.24.0.0", {"start": v(-4.32, 2.8) * mm, "end": v(-3.56, 2.8) * mm});
            skLineSegment(sketch, "E63.24.0.1", {"start": v(-3.56, 2.8) * mm, "end": v(-3.56, 2.03) * mm});
            skLineSegment(sketch, "E63.24.0.2", {"start": v(-4.32, 2.8) * mm, "end": v(-4.32, 2.03) * mm});
            skLineSegment(sketch, "E63.24.0.3", {"start": v(-4.32, 2.03) * mm, "end": v(-3.56, 2.03) * mm});
            skLineSegment(sketch, "E63.25.0.0", {"start": v(-2.8, 2.8) * mm, "end": v(-2.03, 2.8) * mm});
            skLineSegment(sketch, "E63.25.0.1", {"start": v(-2.03, 2.8) * mm, "end": v(-2.03, 2.03) * mm});
            skLineSegment(sketch, "E63.25.0.2", {"start": v(-2.8, 2.8) * mm, "end": v(-2.8, 2.03) * mm});
            skLineSegment(sketch, "E63.25.0.3", {"start": v(-2.8, 2.03) * mm, "end": v(-2.03, 2.03) * mm});
            skLineSegment(sketch, "E63.26.0.0", {"start": v(-1.27, 2.8) * mm, "end": v(-0.5, 2.8) * mm});
            skLineSegment(sketch, "E63.26.0.1", {"start": v(-0.5, 2.8) * mm, "end": v(-0.5, 2.03) * mm});
            skLineSegment(sketch, "E63.26.0.2", {"start": v(-1.27, 2.8) * mm, "end": v(-1.27, 2.03) * mm});
            skLineSegment(sketch, "E63.26.0.3", {"start": v(-1.27, 2.03) * mm, "end": v(-0.5, 2.03) * mm});
            skLineSegment(sketch, "E63.27.0.0", {"start": v(0.25, 2.8) * mm, "end": v(1.02, 2.8) * mm});
            skLineSegment(sketch, "E63.27.0.1", {"start": v(1.02, 2.8) * mm, "end": v(1.02, 2.03) * mm});
            skLineSegment(sketch, "E63.27.0.2", {"start": v(0.25, 2.8) * mm, "end": v(0.25, 2.03) * mm});
            skLineSegment(sketch, "E63.27.0.3", {"start": v(0.25, 2.03) * mm, "end": v(1.02, 2.03) * mm});
            skLineSegment(sketch, "E63.28.0.0", {"start": v(1.78, 2.8) * mm, "end": v(2.54, 2.8) * mm});
            skLineSegment(sketch, "E63.28.0.1", {"start": v(2.54, 2.8) * mm, "end": v(2.54, 2.03) * mm});
            skLineSegment(sketch, "E63.28.0.2", {"start": v(1.78, 2.8) * mm, "end": v(1.78, 2.03) * mm});
            skLineSegment(sketch, "E63.28.0.3", {"start": v(1.78, 2.03) * mm, "end": v(2.54, 2.03) * mm});
            skLineSegment(sketch, "E63.29.0.0", {"start": v(3.3, 2.8) * mm, "end": v(4.06, 2.8) * mm});
            skLineSegment(sketch, "E63.29.0.1", {"start": v(4.06, 2.8) * mm, "end": v(4.06, 2.03) * mm});
            skLineSegment(sketch, "E63.29.0.2", {"start": v(3.3, 2.8) * mm, "end": v(3.3, 2.03) * mm});
            skLineSegment(sketch, "E63.29.0.3", {"start": v(3.3, 2.03) * mm, "end": v(4.06, 2.03) * mm});
            skLineSegment(sketch, "E63.direction1", {"start": v(-40.9, 2.03) * mm, "end": v(-39.37, 2.03) * mm, "construction": true});
            skLineSegment(sketch, "E64.0.30.0", {"start": v(4.83, 2.8) * mm, "end": v(5.59, 2.8) * mm});
            skLineSegment(sketch, "E64.3.30.0", {"start": v(5.59, 2.8) * mm, "end": v(5.59, 2.03) * mm});
            skLineSegment(sketch, "E64.6.30.0", {"start": v(4.83, 2.8) * mm, "end": v(4.83, 2.03) * mm});
            skLineSegment(sketch, "E64.9.30.0", {"start": v(4.83, 2.03) * mm, "end": v(5.59, 2.03) * mm});
            skLineSegment(sketch, "E64.0.31.0", {"start": v(6.35, 2.8) * mm, "end": v(7.11, 2.8) * mm});
            skLineSegment(sketch, "E64.3.31.0", {"start": v(7.11, 2.8) * mm, "end": v(7.11, 2.03) * mm});
            skLineSegment(sketch, "E64.6.31.0", {"start": v(6.35, 2.8) * mm, "end": v(6.35, 2.03) * mm});
            skLineSegment(sketch, "E64.9.31.0", {"start": v(6.35, 2.03) * mm, "end": v(7.11, 2.03) * mm});
            skLineSegment(sketch, "E64.0.32.0", {"start": v(7.87, 2.8) * mm, "end": v(8.64, 2.8) * mm});
            skLineSegment(sketch, "E64.3.32.0", {"start": v(8.64, 2.8) * mm, "end": v(8.64, 2.03) * mm});
            skLineSegment(sketch, "E64.6.32.0", {"start": v(7.87, 2.8) * mm, "end": v(7.87, 2.03) * mm});
            skLineSegment(sketch, "E64.9.32.0", {"start": v(7.87, 2.03) * mm, "end": v(8.64, 2.03) * mm});
            skLineSegment(sketch, "E64.0.33.0", {"start": v(9.4, 2.8) * mm, "end": v(10.16, 2.8) * mm});
            skLineSegment(sketch, "E64.3.33.0", {"start": v(10.16, 2.8) * mm, "end": v(10.16, 2.03) * mm});
            skLineSegment(sketch, "E64.6.33.0", {"start": v(9.4, 2.8) * mm, "end": v(9.4, 2.03) * mm});
            skLineSegment(sketch, "E64.9.33.0", {"start": v(9.4, 2.03) * mm, "end": v(10.16, 2.03) * mm});
            skLineSegment(sketch, "E64.0.34.0", {"start": v(10.92, 2.8) * mm, "end": v(11.68, 2.8) * mm});
            skLineSegment(sketch, "E64.3.34.0", {"start": v(11.68, 2.8) * mm, "end": v(11.68, 2.03) * mm});
            skLineSegment(sketch, "E64.6.34.0", {"start": v(10.92, 2.8) * mm, "end": v(10.92, 2.03) * mm});
            skLineSegment(sketch, "E64.9.34.0", {"start": v(10.92, 2.03) * mm, "end": v(11.68, 2.03) * mm});
            skLineSegment(sketch, "E64.0.35.0", {"start": v(12.45, 2.8) * mm, "end": v(13.2, 2.8) * mm});
            skLineSegment(sketch, "E64.3.35.0", {"start": v(13.2, 2.8) * mm, "end": v(13.2, 2.03) * mm});
            skLineSegment(sketch, "E64.6.35.0", {"start": v(12.45, 2.8) * mm, "end": v(12.45, 2.03) * mm});
            skLineSegment(sketch, "E64.9.35.0", {"start": v(12.45, 2.03) * mm, "end": v(13.2, 2.03) * mm});
            skLineSegment(sketch, "E64.0.36.0", {"start": v(13.97, 2.8) * mm, "end": v(14.73, 2.8) * mm});
            skLineSegment(sketch, "E64.3.36.0", {"start": v(14.73, 2.8) * mm, "end": v(14.73, 2.03) * mm});
            skLineSegment(sketch, "E64.6.36.0", {"start": v(13.97, 2.8) * mm, "end": v(13.97, 2.03) * mm});
            skLineSegment(sketch, "E64.9.36.0", {"start": v(13.97, 2.03) * mm, "end": v(14.73, 2.03) * mm});
            skLineSegment(sketch, "E64.0.37.0", {"start": v(15.5, 2.8) * mm, "end": v(16.26, 2.8) * mm});
            skLineSegment(sketch, "E64.3.37.0", {"start": v(16.26, 2.8) * mm, "end": v(16.26, 2.03) * mm});
            skLineSegment(sketch, "E64.6.37.0", {"start": v(15.5, 2.8) * mm, "end": v(15.5, 2.03) * mm});
            skLineSegment(sketch, "E64.9.37.0", {"start": v(15.5, 2.03) * mm, "end": v(16.26, 2.03) * mm});
            skLineSegment(sketch, "E64.0.38.0", {"start": v(17.02, 2.8) * mm, "end": v(17.78, 2.8) * mm});
            skLineSegment(sketch, "E64.3.38.0", {"start": v(17.78, 2.8) * mm, "end": v(17.78, 2.03) * mm});
            skLineSegment(sketch, "E64.6.38.0", {"start": v(17.02, 2.8) * mm, "end": v(17.02, 2.03) * mm});
            skLineSegment(sketch, "E64.9.38.0", {"start": v(17.02, 2.03) * mm, "end": v(17.78, 2.03) * mm});
            skLineSegment(sketch, "E64.0.39.0", {"start": v(18.54, 2.8) * mm, "end": v(19.3, 2.8) * mm});
            skLineSegment(sketch, "E64.3.39.0", {"start": v(19.3, 2.8) * mm, "end": v(19.3, 2.03) * mm});
            skLineSegment(sketch, "E64.6.39.0", {"start": v(18.54, 2.8) * mm, "end": v(18.54, 2.03) * mm});
            skLineSegment(sketch, "E64.9.39.0", {"start": v(18.54, 2.03) * mm, "end": v(19.3, 2.03) * mm});
            skLineSegment(sketch, "E64.0.40.0", {"start": v(20.07, 2.8) * mm, "end": v(20.83, 2.8) * mm});
            skLineSegment(sketch, "E64.3.40.0", {"start": v(20.83, 2.8) * mm, "end": v(20.83, 2.03) * mm});
            skLineSegment(sketch, "E64.6.40.0", {"start": v(20.07, 2.8) * mm, "end": v(20.07, 2.03) * mm});
            skLineSegment(sketch, "E64.9.40.0", {"start": v(20.07, 2.03) * mm, "end": v(20.83, 2.03) * mm});
            skLineSegment(sketch, "E64.0.41.0", {"start": v(21.59, 2.8) * mm, "end": v(22.35, 2.8) * mm});
            skLineSegment(sketch, "E64.3.41.0", {"start": v(22.35, 2.8) * mm, "end": v(22.35, 2.03) * mm});
            skLineSegment(sketch, "E64.6.41.0", {"start": v(21.59, 2.8) * mm, "end": v(21.59, 2.03) * mm});
            skLineSegment(sketch, "E64.9.41.0", {"start": v(21.59, 2.03) * mm, "end": v(22.35, 2.03) * mm});
            skLineSegment(sketch, "E64.0.42.0", {"start": v(23.11, 2.8) * mm, "end": v(23.88, 2.8) * mm});
            skLineSegment(sketch, "E64.3.42.0", {"start": v(23.88, 2.8) * mm, "end": v(23.88, 2.03) * mm});
            skLineSegment(sketch, "E64.6.42.0", {"start": v(23.11, 2.8) * mm, "end": v(23.11, 2.03) * mm});
            skLineSegment(sketch, "E64.9.42.0", {"start": v(23.11, 2.03) * mm, "end": v(23.88, 2.03) * mm});
            skLineSegment(sketch, "E64.0.43.0", {"start": v(24.64, 2.8) * mm, "end": v(25.4, 2.8) * mm});
            skLineSegment(sketch, "E64.3.43.0", {"start": v(25.4, 2.8) * mm, "end": v(25.4, 2.03) * mm});
            skLineSegment(sketch, "E64.6.43.0", {"start": v(24.64, 2.8) * mm, "end": v(24.64, 2.03) * mm});
            skLineSegment(sketch, "E64.9.43.0", {"start": v(24.64, 2.03) * mm, "end": v(25.4, 2.03) * mm});
            skLineSegment(sketch, "E64.0.44.0", {"start": v(26.16, 2.8) * mm, "end": v(26.92, 2.8) * mm});
            skLineSegment(sketch, "E64.3.44.0", {"start": v(26.92, 2.8) * mm, "end": v(26.92, 2.03) * mm});
            skLineSegment(sketch, "E64.6.44.0", {"start": v(26.16, 2.8) * mm, "end": v(26.16, 2.03) * mm});
            skLineSegment(sketch, "E64.9.44.0", {"start": v(26.16, 2.03) * mm, "end": v(26.92, 2.03) * mm});
            skLineSegment(sketch, "E64.0.45.0", {"start": v(27.69, 2.8) * mm, "end": v(28.45, 2.8) * mm});
            skLineSegment(sketch, "E64.3.45.0", {"start": v(28.45, 2.8) * mm, "end": v(28.45, 2.03) * mm});
            skLineSegment(sketch, "E64.6.45.0", {"start": v(27.69, 2.8) * mm, "end": v(27.69, 2.03) * mm});
            skLineSegment(sketch, "E64.9.45.0", {"start": v(27.69, 2.03) * mm, "end": v(28.45, 2.03) * mm});
            skLineSegment(sketch, "E64.0.46.0", {"start": v(29.2, 2.8) * mm, "end": v(29.97, 2.8) * mm});
            skLineSegment(sketch, "E64.3.46.0", {"start": v(29.97, 2.8) * mm, "end": v(29.97, 2.03) * mm});
            skLineSegment(sketch, "E64.6.46.0", {"start": v(29.2, 2.8) * mm, "end": v(29.2, 2.03) * mm});
            skLineSegment(sketch, "E64.9.46.0", {"start": v(29.2, 2.03) * mm, "end": v(29.97, 2.03) * mm});
            skLineSegment(sketch, "E64.0.47.0", {"start": v(30.73, 2.8) * mm, "end": v(31.5, 2.8) * mm});
            skLineSegment(sketch, "E64.3.47.0", {"start": v(31.5, 2.8) * mm, "end": v(31.5, 2.03) * mm});
            skLineSegment(sketch, "E64.6.47.0", {"start": v(30.73, 2.8) * mm, "end": v(30.73, 2.03) * mm});
            skLineSegment(sketch, "E64.9.47.0", {"start": v(30.73, 2.03) * mm, "end": v(31.5, 2.03) * mm});
            skLineSegment(sketch, "E64.0.48.0", {"start": v(32.26, 2.8) * mm, "end": v(33.02, 2.8) * mm});
            skLineSegment(sketch, "E64.3.48.0", {"start": v(33.02, 2.8) * mm, "end": v(33.02, 2.03) * mm});
            skLineSegment(sketch, "E64.6.48.0", {"start": v(32.26, 2.8) * mm, "end": v(32.26, 2.03) * mm});
            skLineSegment(sketch, "E64.9.48.0", {"start": v(32.26, 2.03) * mm, "end": v(33.02, 2.03) * mm});
            skLineSegment(sketch, "E64.0.49.0", {"start": v(33.78, 2.8) * mm, "end": v(34.54, 2.8) * mm});
            skLineSegment(sketch, "E64.3.49.0", {"start": v(34.54, 2.8) * mm, "end": v(34.54, 2.03) * mm});
            skLineSegment(sketch, "E64.6.49.0", {"start": v(33.78, 2.8) * mm, "end": v(33.78, 2.03) * mm});
            skLineSegment(sketch, "E64.9.49.0", {"start": v(33.78, 2.03) * mm, "end": v(34.54, 2.03) * mm});
            skLineSegment(sketch, "E65.0.50.0", {"start": v(35.3, 2.8) * mm, "end": v(36.07, 2.8) * mm});
            skLineSegment(sketch, "E65.3.50.0", {"start": v(36.07, 2.8) * mm, "end": v(36.07, 2.03) * mm});
            skLineSegment(sketch, "E65.6.50.0", {"start": v(35.3, 2.8) * mm, "end": v(35.3, 2.03) * mm});
            skLineSegment(sketch, "E65.9.50.0", {"start": v(35.3, 2.03) * mm, "end": v(36.07, 2.03) * mm});
            skLineSegment(sketch, "E65.0.51.0", {"start": v(36.83, 2.8) * mm, "end": v(37.6, 2.8) * mm});
            skLineSegment(sketch, "E65.3.51.0", {"start": v(37.6, 2.8) * mm, "end": v(37.6, 2.03) * mm});
            skLineSegment(sketch, "E65.6.51.0", {"start": v(36.83, 2.8) * mm, "end": v(36.83, 2.03) * mm});
            skLineSegment(sketch, "E65.9.51.0", {"start": v(36.83, 2.03) * mm, "end": v(37.6, 2.03) * mm});
            skLineSegment(sketch, "E65.0.52.0", {"start": v(38.35, 2.8) * mm, "end": v(39.12, 2.8) * mm});
            skLineSegment(sketch, "E65.3.52.0", {"start": v(39.12, 2.8) * mm, "end": v(39.12, 2.03) * mm});
            skLineSegment(sketch, "E65.6.52.0", {"start": v(38.35, 2.8) * mm, "end": v(38.35, 2.03) * mm});
            skLineSegment(sketch, "E65.9.52.0", {"start": v(38.35, 2.03) * mm, "end": v(39.12, 2.03) * mm});
            skLineSegment(sketch, "E65.0.53.0", {"start": v(39.88, 2.8) * mm, "end": v(40.64, 2.8) * mm});
            skLineSegment(sketch, "E65.3.53.0", {"start": v(40.64, 2.8) * mm, "end": v(40.64, 2.03) * mm});
            skLineSegment(sketch, "E65.6.53.0", {"start": v(39.88, 2.8) * mm, "end": v(39.88, 2.03) * mm});
            skLineSegment(sketch, "E65.9.53.0", {"start": v(39.88, 2.03) * mm, "end": v(40.64, 2.03) * mm});
            skSolve(sketch);
        }
        {
            var Q0;
            Q0 = qSketchRegion(id + "F26", true);
            extrude(context, id + "F27", {"entities" : qUnion([Q0]), "operationType" : NewBodyOperationType.REMOVE, "endBound" : BoundingType.UP_TO_NEXT, "oppositeDirection" : true, "depth" : 1.52 * mm});
        }
        {
            var Q0;
            Q0=makeQuery(id+"F4.opExtrude","SWEPT_FACE",FACE,{"disambiguationData":[OSD([sQuery(id+"F3.wireOp",EDGE,"E5.top")])]});
            var sketch = newSketch(context, id + "F28", { "sketchPlane" : qUnion([Q0])});
            skLineSegment(sketch, "E66.bottom", {"start": v(-42.42, 12.2) * mm, "end": v(-41.66, 12.2) * mm});
            skLineSegment(sketch, "E66.top", {"start": v(-42.42, 2.03) * mm, "end": v(-41.66, 2.03) * mm});
            skLineSegment(sketch, "E66.left", {"start": v(-42.42, 12.2) * mm, "end": v(-42.42, 2.03) * mm});
            skLineSegment(sketch, "E66.right", {"start": v(-41.66, 12.2) * mm, "end": v(-41.66, 2.03) * mm});
            skLineSegment(sketch, "E67.0.1.0", {"start": v(-42.42, 23.62) * mm, "end": v(-42.42, 13.46) * mm});
            skLineSegment(sketch, "E67.0.1.1", {"start": v(-41.66, 23.62) * mm, "end": v(-41.66, 13.46) * mm});
            skLineSegment(sketch, "E67.0.1.2", {"start": v(-42.42, 23.62) * mm, "end": v(-41.66, 23.62) * mm});
            skLineSegment(sketch, "E67.0.1.3", {"start": v(-42.42, 13.46) * mm, "end": v(-41.66, 13.46) * mm});
            skLineSegment(sketch, "E67.0.2.0", {"start": v(-42.42, 35.05) * mm, "end": v(-42.42, 24.9) * mm});
            skLineSegment(sketch, "E67.0.2.1", {"start": v(-41.66, 35.05) * mm, "end": v(-41.66, 24.9) * mm});
            skLineSegment(sketch, "E67.0.2.2", {"start": v(-42.42, 35.05) * mm, "end": v(-41.66, 35.05) * mm});
            skLineSegment(sketch, "E67.0.2.3", {"start": v(-42.42, 24.9) * mm, "end": v(-41.66, 24.9) * mm});
            skLineSegment(sketch, "E67.0.3.0", {"start": v(-42.42, 46.48) * mm, "end": v(-42.42, 36.32) * mm});
            skLineSegment(sketch, "E67.0.3.1", {"start": v(-41.66, 46.48) * mm, "end": v(-41.66, 36.32) * mm});
            skLineSegment(sketch, "E67.0.3.2", {"start": v(-42.42, 46.48) * mm, "end": v(-41.66, 46.48) * mm});
            skLineSegment(sketch, "E67.0.3.3", {"start": v(-42.42, 36.32) * mm, "end": v(-41.66, 36.32) * mm});
            skLineSegment(sketch, "E67.0.4.0", {"start": v(-42.42, 57.91) * mm, "end": v(-42.42, 47.75) * mm});
            skLineSegment(sketch, "E67.0.4.1", {"start": v(-41.66, 57.91) * mm, "end": v(-41.66, 47.75) * mm});
            skLineSegment(sketch, "E67.0.4.2", {"start": v(-42.42, 57.91) * mm, "end": v(-41.66, 57.91) * mm});
            skLineSegment(sketch, "E67.0.4.3", {"start": v(-42.42, 47.75) * mm, "end": v(-41.66, 47.75) * mm});
            skLineSegment(sketch, "E67.direction1", {"start": v(-44.5, 2.03) * mm, "end": v(-42.42, 2.03) * mm, "construction": true});
            skLineSegment(sketch, "E67.direction2", {"start": v(-42.42, 2.03) * mm, "end": v(-42.42, 13.46) * mm, "construction": true});
            skLineSegment(sketch, "E68.1.0.0", {"start": v(42.42, 35.05) * mm, "end": v(42.42, 24.9) * mm});
            skLineSegment(sketch, "E68.1.0.1", {"start": v(41.66, 35.05) * mm, "end": v(41.66, 24.9) * mm});
            skLineSegment(sketch, "E68.1.0.3", {"start": v(41.66, 57.91) * mm, "end": v(41.66, 47.75) * mm});
            skLineSegment(sketch, "E68.1.0.12", {"start": v(41.66, 23.62) * mm, "end": v(41.66, 13.46) * mm});
            skLineSegment(sketch, "E68.1.0.19", {"start": v(42.42, 12.2) * mm, "end": v(42.42, 2.03) * mm});
            skLineSegment(sketch, "E68.1.0.20", {"start": v(41.66, 46.48) * mm, "end": v(41.66, 36.32) * mm});
            skLineSegment(sketch, "E68.1.0.21", {"start": v(42.42, 46.48) * mm, "end": v(42.42, 36.32) * mm});
            skLineSegment(sketch, "E68.1.0.22", {"start": v(41.66, 2.03) * mm, "end": v(41.66, 13.46) * mm, "construction": true});
            skLineSegment(sketch, "E68.1.0.26", {"start": v(39.57, 2.03) * mm, "end": v(41.66, 2.03) * mm, "construction": true});
            skLineSegment(sketch, "E68.1.0.29", {"start": v(42.42, 57.91) * mm, "end": v(42.42, 47.75) * mm});
            skLineSegment(sketch, "E68.1.0.30", {"start": v(42.42, 23.62) * mm, "end": v(42.42, 13.46) * mm});
            skLineSegment(sketch, "E68.1.0.31", {"start": v(41.66, 12.2) * mm, "end": v(41.66, 2.03) * mm});
            skLineSegment(sketch, "E68.1.0.32", {"start": v(41.66, 13.46) * mm, "end": v(42.42, 13.46) * mm});
            skLineSegment(sketch, "E68.1.0.33", {"start": v(41.66, 23.62) * mm, "end": v(42.42, 23.62) * mm});
            skLineSegment(sketch, "E68.1.0.50", {"start": v(41.66, 57.91) * mm, "end": v(42.42, 57.91) * mm});
            skLineSegment(sketch, "E68.1.0.53", {"start": v(41.66, 2.03) * mm, "end": v(42.42, 2.03) * mm});
            skLineSegment(sketch, "E68.1.0.54", {"start": v(41.66, 12.2) * mm, "end": v(42.42, 12.2) * mm});
            skLineSegment(sketch, "E68.1.0.55", {"start": v(41.66, 36.32) * mm, "end": v(42.42, 36.32) * mm});
            skLineSegment(sketch, "E68.1.0.56", {"start": v(41.66, 47.75) * mm, "end": v(42.42, 47.75) * mm});
            skLineSegment(sketch, "E68.1.0.59", {"start": v(41.66, 24.9) * mm, "end": v(42.42, 24.9) * mm});
            skLineSegment(sketch, "E68.1.0.60", {"start": v(41.66, 35.05) * mm, "end": v(42.42, 35.05) * mm});
            skLineSegment(sketch, "E68.1.0.61", {"start": v(41.66, 46.48) * mm, "end": v(42.42, 46.48) * mm});
            skLineSegment(sketch, "E68.direction1", {"start": v(-42.42, 2.03) * mm, "end": v(41.66, 2.03) * mm, "construction": true});
            skLineSegment(sketch, "E69.bottom", {"start": v(-40.9, 2.8) * mm, "end": v(-40.13, 2.8) * mm});
            skLineSegment(sketch, "E69.top", {"start": v(-40.9, 2.03) * mm, "end": v(-40.13, 2.03) * mm});
            skLineSegment(sketch, "E69.left", {"start": v(-40.9, 2.8) * mm, "end": v(-40.9, 2.03) * mm});
            skLineSegment(sketch, "E69.right", {"start": v(-40.13, 2.8) * mm, "end": v(-40.13, 2.03) * mm});
            skLineSegment(sketch, "E70.1.0.0", {"start": v(-39.37, 2.8) * mm, "end": v(-38.6, 2.8) * mm});
            skLineSegment(sketch, "E70.1.0.1", {"start": v(-38.6, 2.8) * mm, "end": v(-38.6, 2.03) * mm});
            skLineSegment(sketch, "E70.1.0.2", {"start": v(-39.37, 2.8) * mm, "end": v(-39.37, 2.03) * mm});
            skLineSegment(sketch, "E70.1.0.3", {"start": v(-39.37, 2.03) * mm, "end": v(-38.6, 2.03) * mm});
            skLineSegment(sketch, "E70.2.0.0", {"start": v(-37.85, 2.8) * mm, "end": v(-37.08, 2.8) * mm});
            skLineSegment(sketch, "E70.2.0.1", {"start": v(-37.08, 2.8) * mm, "end": v(-37.08, 2.03) * mm});
            skLineSegment(sketch, "E70.2.0.2", {"start": v(-37.85, 2.8) * mm, "end": v(-37.85, 2.03) * mm});
            skLineSegment(sketch, "E70.2.0.3", {"start": v(-37.85, 2.03) * mm, "end": v(-37.08, 2.03) * mm});
            skLineSegment(sketch, "E70.3.0.0", {"start": v(-36.32, 2.8) * mm, "end": v(-35.56, 2.8) * mm});
            skLineSegment(sketch, "E70.3.0.1", {"start": v(-35.56, 2.8) * mm, "end": v(-35.56, 2.03) * mm});
            skLineSegment(sketch, "E70.3.0.2", {"start": v(-36.32, 2.8) * mm, "end": v(-36.32, 2.03) * mm});
            skLineSegment(sketch, "E70.3.0.3", {"start": v(-36.32, 2.03) * mm, "end": v(-35.56, 2.03) * mm});
            skLineSegment(sketch, "E70.4.0.0", {"start": v(-34.8, 2.8) * mm, "end": v(-34.04, 2.8) * mm});
            skLineSegment(sketch, "E70.4.0.1", {"start": v(-34.04, 2.8) * mm, "end": v(-34.04, 2.03) * mm});
            skLineSegment(sketch, "E70.4.0.2", {"start": v(-34.8, 2.8) * mm, "end": v(-34.8, 2.03) * mm});
            skLineSegment(sketch, "E70.4.0.3", {"start": v(-34.8, 2.03) * mm, "end": v(-34.04, 2.03) * mm});
            skLineSegment(sketch, "E70.5.0.0", {"start": v(-33.27, 2.8) * mm, "end": v(-32.51, 2.8) * mm});
            skLineSegment(sketch, "E70.5.0.1", {"start": v(-32.51, 2.8) * mm, "end": v(-32.51, 2.03) * mm});
            skLineSegment(sketch, "E70.5.0.2", {"start": v(-33.27, 2.8) * mm, "end": v(-33.27, 2.03) * mm});
            skLineSegment(sketch, "E70.5.0.3", {"start": v(-33.27, 2.03) * mm, "end": v(-32.51, 2.03) * mm});
            skLineSegment(sketch, "E70.6.0.0", {"start": v(-31.75, 2.8) * mm, "end": v(-30.99, 2.8) * mm});
            skLineSegment(sketch, "E70.6.0.1", {"start": v(-30.99, 2.8) * mm, "end": v(-30.99, 2.03) * mm});
            skLineSegment(sketch, "E70.6.0.2", {"start": v(-31.75, 2.8) * mm, "end": v(-31.75, 2.03) * mm});
            skLineSegment(sketch, "E70.6.0.3", {"start": v(-31.75, 2.03) * mm, "end": v(-30.99, 2.03) * mm});
            skLineSegment(sketch, "E70.7.0.0", {"start": v(-30.23, 2.8) * mm, "end": v(-29.46, 2.8) * mm});
            skLineSegment(sketch, "E70.7.0.1", {"start": v(-29.46, 2.8) * mm, "end": v(-29.46, 2.03) * mm});
            skLineSegment(sketch, "E70.7.0.2", {"start": v(-30.23, 2.8) * mm, "end": v(-30.23, 2.03) * mm});
            skLineSegment(sketch, "E70.7.0.3", {"start": v(-30.23, 2.03) * mm, "end": v(-29.46, 2.03) * mm});
            skLineSegment(sketch, "E70.8.0.0", {"start": v(-28.7, 2.8) * mm, "end": v(-27.94, 2.8) * mm});
            skLineSegment(sketch, "E70.8.0.1", {"start": v(-27.94, 2.8) * mm, "end": v(-27.94, 2.03) * mm});
            skLineSegment(sketch, "E70.8.0.2", {"start": v(-28.7, 2.8) * mm, "end": v(-28.7, 2.03) * mm});
            skLineSegment(sketch, "E70.8.0.3", {"start": v(-28.7, 2.03) * mm, "end": v(-27.94, 2.03) * mm});
            skLineSegment(sketch, "E70.9.0.0", {"start": v(-27.18, 2.8) * mm, "end": v(-26.42, 2.8) * mm});
            skLineSegment(sketch, "E70.9.0.1", {"start": v(-26.42, 2.8) * mm, "end": v(-26.42, 2.03) * mm});
            skLineSegment(sketch, "E70.9.0.2", {"start": v(-27.18, 2.8) * mm, "end": v(-27.18, 2.03) * mm});
            skLineSegment(sketch, "E70.9.0.3", {"start": v(-27.18, 2.03) * mm, "end": v(-26.42, 2.03) * mm});
            skLineSegment(sketch, "E70.10.0.0", {"start": v(-25.65, 2.8) * mm, "end": v(-24.9, 2.8) * mm});
            skLineSegment(sketch, "E70.10.0.1", {"start": v(-24.9, 2.8) * mm, "end": v(-24.9, 2.03) * mm});
            skLineSegment(sketch, "E70.10.0.2", {"start": v(-25.65, 2.8) * mm, "end": v(-25.65, 2.03) * mm});
            skLineSegment(sketch, "E70.10.0.3", {"start": v(-25.65, 2.03) * mm, "end": v(-24.9, 2.03) * mm});
            skLineSegment(sketch, "E70.11.0.0", {"start": v(-24.13, 2.8) * mm, "end": v(-23.37, 2.8) * mm});
            skLineSegment(sketch, "E70.11.0.1", {"start": v(-23.37, 2.8) * mm, "end": v(-23.37, 2.03) * mm});
            skLineSegment(sketch, "E70.11.0.2", {"start": v(-24.13, 2.8) * mm, "end": v(-24.13, 2.03) * mm});
            skLineSegment(sketch, "E70.11.0.3", {"start": v(-24.13, 2.03) * mm, "end": v(-23.37, 2.03) * mm});
            skLineSegment(sketch, "E70.12.0.0", {"start": v(-22.6, 2.8) * mm, "end": v(-21.84, 2.8) * mm});
            skLineSegment(sketch, "E70.12.0.1", {"start": v(-21.84, 2.8) * mm, "end": v(-21.84, 2.03) * mm});
            skLineSegment(sketch, "E70.12.0.2", {"start": v(-22.6, 2.8) * mm, "end": v(-22.6, 2.03) * mm});
            skLineSegment(sketch, "E70.12.0.3", {"start": v(-22.6, 2.03) * mm, "end": v(-21.84, 2.03) * mm});
            skLineSegment(sketch, "E70.13.0.0", {"start": v(-21.08, 2.8) * mm, "end": v(-20.32, 2.8) * mm});
            skLineSegment(sketch, "E70.13.0.1", {"start": v(-20.32, 2.8) * mm, "end": v(-20.32, 2.03) * mm});
            skLineSegment(sketch, "E70.13.0.2", {"start": v(-21.08, 2.8) * mm, "end": v(-21.08, 2.03) * mm});
            skLineSegment(sketch, "E70.13.0.3", {"start": v(-21.08, 2.03) * mm, "end": v(-20.32, 2.03) * mm});
            skLineSegment(sketch, "E70.14.0.0", {"start": v(-19.56, 2.8) * mm, "end": v(-18.8, 2.8) * mm});
            skLineSegment(sketch, "E70.14.0.1", {"start": v(-18.8, 2.8) * mm, "end": v(-18.8, 2.03) * mm});
            skLineSegment(sketch, "E70.14.0.2", {"start": v(-19.56, 2.8) * mm, "end": v(-19.56, 2.03) * mm});
            skLineSegment(sketch, "E70.14.0.3", {"start": v(-19.56, 2.03) * mm, "end": v(-18.8, 2.03) * mm});
            skLineSegment(sketch, "E70.15.0.0", {"start": v(-18.03, 2.8) * mm, "end": v(-17.27, 2.8) * mm});
            skLineSegment(sketch, "E70.15.0.1", {"start": v(-17.27, 2.8) * mm, "end": v(-17.27, 2.03) * mm});
            skLineSegment(sketch, "E70.15.0.2", {"start": v(-18.03, 2.8) * mm, "end": v(-18.03, 2.03) * mm});
            skLineSegment(sketch, "E70.15.0.3", {"start": v(-18.03, 2.03) * mm, "end": v(-17.27, 2.03) * mm});
            skLineSegment(sketch, "E70.16.0.0", {"start": v(-16.5, 2.8) * mm, "end": v(-15.75, 2.8) * mm});
            skLineSegment(sketch, "E70.16.0.1", {"start": v(-15.75, 2.8) * mm, "end": v(-15.75, 2.03) * mm});
            skLineSegment(sketch, "E70.16.0.2", {"start": v(-16.5, 2.8) * mm, "end": v(-16.5, 2.03) * mm});
            skLineSegment(sketch, "E70.16.0.3", {"start": v(-16.5, 2.03) * mm, "end": v(-15.75, 2.03) * mm});
            skLineSegment(sketch, "E70.17.0.0", {"start": v(-14.99, 2.8) * mm, "end": v(-14.22, 2.8) * mm});
            skLineSegment(sketch, "E70.17.0.1", {"start": v(-14.22, 2.8) * mm, "end": v(-14.22, 2.03) * mm});
            skLineSegment(sketch, "E70.17.0.2", {"start": v(-14.99, 2.8) * mm, "end": v(-14.99, 2.03) * mm});
            skLineSegment(sketch, "E70.17.0.3", {"start": v(-14.99, 2.03) * mm, "end": v(-14.22, 2.03) * mm});
            skLineSegment(sketch, "E70.18.0.0", {"start": v(-13.46, 2.8) * mm, "end": v(-12.7, 2.8) * mm});
            skLineSegment(sketch, "E70.18.0.1", {"start": v(-12.7, 2.8) * mm, "end": v(-12.7, 2.03) * mm});
            skLineSegment(sketch, "E70.18.0.2", {"start": v(-13.46, 2.8) * mm, "end": v(-13.46, 2.03) * mm});
            skLineSegment(sketch, "E70.18.0.3", {"start": v(-13.46, 2.03) * mm, "end": v(-12.7, 2.03) * mm});
            skLineSegment(sketch, "E70.19.0.0", {"start": v(-11.94, 2.8) * mm, "end": v(-11.18, 2.8) * mm});
            skLineSegment(sketch, "E70.19.0.1", {"start": v(-11.18, 2.8) * mm, "end": v(-11.18, 2.03) * mm});
            skLineSegment(sketch, "E70.19.0.2", {"start": v(-11.94, 2.8) * mm, "end": v(-11.94, 2.03) * mm});
            skLineSegment(sketch, "E70.19.0.3", {"start": v(-11.94, 2.03) * mm, "end": v(-11.18, 2.03) * mm});
            skLineSegment(sketch, "E70.20.0.0", {"start": v(-10.41, 2.8) * mm, "end": v(-9.65, 2.8) * mm});
            skLineSegment(sketch, "E70.20.0.1", {"start": v(-9.65, 2.8) * mm, "end": v(-9.65, 2.03) * mm});
            skLineSegment(sketch, "E70.20.0.2", {"start": v(-10.41, 2.8) * mm, "end": v(-10.41, 2.03) * mm});
            skLineSegment(sketch, "E70.20.0.3", {"start": v(-10.41, 2.03) * mm, "end": v(-9.65, 2.03) * mm});
            skLineSegment(sketch, "E70.21.0.0", {"start": v(-8.89, 2.8) * mm, "end": v(-8.13, 2.8) * mm});
            skLineSegment(sketch, "E70.21.0.1", {"start": v(-8.13, 2.8) * mm, "end": v(-8.13, 2.03) * mm});
            skLineSegment(sketch, "E70.21.0.2", {"start": v(-8.89, 2.8) * mm, "end": v(-8.89, 2.03) * mm});
            skLineSegment(sketch, "E70.21.0.3", {"start": v(-8.89, 2.03) * mm, "end": v(-8.13, 2.03) * mm});
            skLineSegment(sketch, "E70.22.0.0", {"start": v(-7.37, 2.8) * mm, "end": v(-6.6, 2.8) * mm});
            skLineSegment(sketch, "E70.22.0.1", {"start": v(-6.6, 2.8) * mm, "end": v(-6.6, 2.03) * mm});
            skLineSegment(sketch, "E70.22.0.2", {"start": v(-7.37, 2.8) * mm, "end": v(-7.37, 2.03) * mm});
            skLineSegment(sketch, "E70.22.0.3", {"start": v(-7.37, 2.03) * mm, "end": v(-6.6, 2.03) * mm});
            skLineSegment(sketch, "E70.23.0.0", {"start": v(-5.84, 2.8) * mm, "end": v(-5.08, 2.8) * mm});
            skLineSegment(sketch, "E70.23.0.1", {"start": v(-5.08, 2.8) * mm, "end": v(-5.08, 2.03) * mm});
            skLineSegment(sketch, "E70.23.0.2", {"start": v(-5.84, 2.8) * mm, "end": v(-5.84, 2.03) * mm});
            skLineSegment(sketch, "E70.23.0.3", {"start": v(-5.84, 2.03) * mm, "end": v(-5.08, 2.03) * mm});
            skLineSegment(sketch, "E70.24.0.0", {"start": v(-4.32, 2.8) * mm, "end": v(-3.56, 2.8) * mm});
            skLineSegment(sketch, "E70.24.0.1", {"start": v(-3.56, 2.8) * mm, "end": v(-3.56, 2.03) * mm});
            skLineSegment(sketch, "E70.24.0.2", {"start": v(-4.32, 2.8) * mm, "end": v(-4.32, 2.03) * mm});
            skLineSegment(sketch, "E70.24.0.3", {"start": v(-4.32, 2.03) * mm, "end": v(-3.56, 2.03) * mm});
            skLineSegment(sketch, "E70.25.0.0", {"start": v(-2.8, 2.8) * mm, "end": v(-2.03, 2.8) * mm});
            skLineSegment(sketch, "E70.25.0.1", {"start": v(-2.03, 2.8) * mm, "end": v(-2.03, 2.03) * mm});
            skLineSegment(sketch, "E70.25.0.2", {"start": v(-2.8, 2.8) * mm, "end": v(-2.8, 2.03) * mm});
            skLineSegment(sketch, "E70.25.0.3", {"start": v(-2.8, 2.03) * mm, "end": v(-2.03, 2.03) * mm});
            skLineSegment(sketch, "E70.26.0.0", {"start": v(-1.27, 2.8) * mm, "end": v(-0.5, 2.8) * mm});
            skLineSegment(sketch, "E70.26.0.1", {"start": v(-0.5, 2.8) * mm, "end": v(-0.5, 2.03) * mm});
            skLineSegment(sketch, "E70.26.0.2", {"start": v(-1.27, 2.8) * mm, "end": v(-1.27, 2.03) * mm});
            skLineSegment(sketch, "E70.26.0.3", {"start": v(-1.27, 2.03) * mm, "end": v(-0.5, 2.03) * mm});
            skLineSegment(sketch, "E70.27.0.0", {"start": v(0.25, 2.8) * mm, "end": v(1.02, 2.8) * mm});
            skLineSegment(sketch, "E70.27.0.1", {"start": v(1.02, 2.8) * mm, "end": v(1.02, 2.03) * mm});
            skLineSegment(sketch, "E70.27.0.2", {"start": v(0.25, 2.8) * mm, "end": v(0.25, 2.03) * mm});
            skLineSegment(sketch, "E70.27.0.3", {"start": v(0.25, 2.03) * mm, "end": v(1.02, 2.03) * mm});
            skLineSegment(sketch, "E70.28.0.0", {"start": v(1.78, 2.8) * mm, "end": v(2.54, 2.8) * mm});
            skLineSegment(sketch, "E70.28.0.1", {"start": v(2.54, 2.8) * mm, "end": v(2.54, 2.03) * mm});
            skLineSegment(sketch, "E70.28.0.2", {"start": v(1.78, 2.8) * mm, "end": v(1.78, 2.03) * mm});
            skLineSegment(sketch, "E70.28.0.3", {"start": v(1.78, 2.03) * mm, "end": v(2.54, 2.03) * mm});
            skLineSegment(sketch, "E70.29.0.0", {"start": v(3.3, 2.8) * mm, "end": v(4.06, 2.8) * mm});
            skLineSegment(sketch, "E70.29.0.1", {"start": v(4.06, 2.8) * mm, "end": v(4.06, 2.03) * mm});
            skLineSegment(sketch, "E70.29.0.2", {"start": v(3.3, 2.8) * mm, "end": v(3.3, 2.03) * mm});
            skLineSegment(sketch, "E70.29.0.3", {"start": v(3.3, 2.03) * mm, "end": v(4.06, 2.03) * mm});
            skLineSegment(sketch, "E70.direction1", {"start": v(-40.9, 2.03) * mm, "end": v(-39.37, 2.03) * mm, "construction": true});
            skLineSegment(sketch, "E71.0.30.0", {"start": v(4.83, 2.8) * mm, "end": v(5.59, 2.8) * mm});
            skLineSegment(sketch, "E71.3.30.0", {"start": v(5.59, 2.8) * mm, "end": v(5.59, 2.03) * mm});
            skLineSegment(sketch, "E71.6.30.0", {"start": v(4.83, 2.8) * mm, "end": v(4.83, 2.03) * mm});
            skLineSegment(sketch, "E71.9.30.0", {"start": v(4.83, 2.03) * mm, "end": v(5.59, 2.03) * mm});
            skLineSegment(sketch, "E71.0.31.0", {"start": v(6.35, 2.8) * mm, "end": v(7.11, 2.8) * mm});
            skLineSegment(sketch, "E71.3.31.0", {"start": v(7.11, 2.8) * mm, "end": v(7.11, 2.03) * mm});
            skLineSegment(sketch, "E71.6.31.0", {"start": v(6.35, 2.8) * mm, "end": v(6.35, 2.03) * mm});
            skLineSegment(sketch, "E71.9.31.0", {"start": v(6.35, 2.03) * mm, "end": v(7.11, 2.03) * mm});
            skLineSegment(sketch, "E71.0.32.0", {"start": v(7.87, 2.8) * mm, "end": v(8.64, 2.8) * mm});
            skLineSegment(sketch, "E71.3.32.0", {"start": v(8.64, 2.8) * mm, "end": v(8.64, 2.03) * mm});
            skLineSegment(sketch, "E71.6.32.0", {"start": v(7.87, 2.8) * mm, "end": v(7.87, 2.03) * mm});
            skLineSegment(sketch, "E71.9.32.0", {"start": v(7.87, 2.03) * mm, "end": v(8.64, 2.03) * mm});
            skLineSegment(sketch, "E71.0.33.0", {"start": v(9.4, 2.8) * mm, "end": v(10.16, 2.8) * mm});
            skLineSegment(sketch, "E71.3.33.0", {"start": v(10.16, 2.8) * mm, "end": v(10.16, 2.03) * mm});
            skLineSegment(sketch, "E71.6.33.0", {"start": v(9.4, 2.8) * mm, "end": v(9.4, 2.03) * mm});
            skLineSegment(sketch, "E71.9.33.0", {"start": v(9.4, 2.03) * mm, "end": v(10.16, 2.03) * mm});
            skLineSegment(sketch, "E71.0.34.0", {"start": v(10.92, 2.8) * mm, "end": v(11.68, 2.8) * mm});
            skLineSegment(sketch, "E71.3.34.0", {"start": v(11.68, 2.8) * mm, "end": v(11.68, 2.03) * mm});
            skLineSegment(sketch, "E71.6.34.0", {"start": v(10.92, 2.8) * mm, "end": v(10.92, 2.03) * mm});
            skLineSegment(sketch, "E71.9.34.0", {"start": v(10.92, 2.03) * mm, "end": v(11.68, 2.03) * mm});
            skLineSegment(sketch, "E71.0.35.0", {"start": v(12.45, 2.8) * mm, "end": v(13.2, 2.8) * mm});
            skLineSegment(sketch, "E71.3.35.0", {"start": v(13.2, 2.8) * mm, "end": v(13.2, 2.03) * mm});
            skLineSegment(sketch, "E71.6.35.0", {"start": v(12.45, 2.8) * mm, "end": v(12.45, 2.03) * mm});
            skLineSegment(sketch, "E71.9.35.0", {"start": v(12.45, 2.03) * mm, "end": v(13.2, 2.03) * mm});
            skLineSegment(sketch, "E71.0.36.0", {"start": v(13.97, 2.8) * mm, "end": v(14.73, 2.8) * mm});
            skLineSegment(sketch, "E71.3.36.0", {"start": v(14.73, 2.8) * mm, "end": v(14.73, 2.03) * mm});
            skLineSegment(sketch, "E71.6.36.0", {"start": v(13.97, 2.8) * mm, "end": v(13.97, 2.03) * mm});
            skLineSegment(sketch, "E71.9.36.0", {"start": v(13.97, 2.03) * mm, "end": v(14.73, 2.03) * mm});
            skLineSegment(sketch, "E71.0.37.0", {"start": v(15.5, 2.8) * mm, "end": v(16.26, 2.8) * mm});
            skLineSegment(sketch, "E71.3.37.0", {"start": v(16.26, 2.8) * mm, "end": v(16.26, 2.03) * mm});
            skLineSegment(sketch, "E71.6.37.0", {"start": v(15.5, 2.8) * mm, "end": v(15.5, 2.03) * mm});
            skLineSegment(sketch, "E71.9.37.0", {"start": v(15.5, 2.03) * mm, "end": v(16.26, 2.03) * mm});
            skLineSegment(sketch, "E71.0.38.0", {"start": v(17.02, 2.8) * mm, "end": v(17.78, 2.8) * mm});
            skLineSegment(sketch, "E71.3.38.0", {"start": v(17.78, 2.8) * mm, "end": v(17.78, 2.03) * mm});
            skLineSegment(sketch, "E71.6.38.0", {"start": v(17.02, 2.8) * mm, "end": v(17.02, 2.03) * mm});
            skLineSegment(sketch, "E71.9.38.0", {"start": v(17.02, 2.03) * mm, "end": v(17.78, 2.03) * mm});
            skLineSegment(sketch, "E71.0.39.0", {"start": v(18.54, 2.8) * mm, "end": v(19.3, 2.8) * mm});
            skLineSegment(sketch, "E71.3.39.0", {"start": v(19.3, 2.8) * mm, "end": v(19.3, 2.03) * mm});
            skLineSegment(sketch, "E71.6.39.0", {"start": v(18.54, 2.8) * mm, "end": v(18.54, 2.03) * mm});
            skLineSegment(sketch, "E71.9.39.0", {"start": v(18.54, 2.03) * mm, "end": v(19.3, 2.03) * mm});
            skLineSegment(sketch, "E71.0.40.0", {"start": v(20.07, 2.8) * mm, "end": v(20.83, 2.8) * mm});
            skLineSegment(sketch, "E71.3.40.0", {"start": v(20.83, 2.8) * mm, "end": v(20.83, 2.03) * mm});
            skLineSegment(sketch, "E71.6.40.0", {"start": v(20.07, 2.8) * mm, "end": v(20.07, 2.03) * mm});
            skLineSegment(sketch, "E71.9.40.0", {"start": v(20.07, 2.03) * mm, "end": v(20.83, 2.03) * mm});
            skLineSegment(sketch, "E71.0.41.0", {"start": v(21.6, 2.8) * mm, "end": v(22.35, 2.8) * mm});
            skLineSegment(sketch, "E71.3.41.0", {"start": v(22.35, 2.8) * mm, "end": v(22.35, 2.03) * mm});
            skLineSegment(sketch, "E71.6.41.0", {"start": v(21.6, 2.8) * mm, "end": v(21.6, 2.03) * mm});
            skLineSegment(sketch, "E71.9.41.0", {"start": v(21.6, 2.03) * mm, "end": v(22.35, 2.03) * mm});
            skLineSegment(sketch, "E71.0.42.0", {"start": v(23.11, 2.8) * mm, "end": v(23.88, 2.8) * mm});
            skLineSegment(sketch, "E71.3.42.0", {"start": v(23.88, 2.8) * mm, "end": v(23.88, 2.03) * mm});
            skLineSegment(sketch, "E71.6.42.0", {"start": v(23.11, 2.8) * mm, "end": v(23.11, 2.03) * mm});
            skLineSegment(sketch, "E71.9.42.0", {"start": v(23.11, 2.03) * mm, "end": v(23.88, 2.03) * mm});
            skLineSegment(sketch, "E71.0.43.0", {"start": v(24.64, 2.8) * mm, "end": v(25.4, 2.8) * mm});
            skLineSegment(sketch, "E71.3.43.0", {"start": v(25.4, 2.8) * mm, "end": v(25.4, 2.03) * mm});
            skLineSegment(sketch, "E71.6.43.0", {"start": v(24.64, 2.8) * mm, "end": v(24.64, 2.03) * mm});
            skLineSegment(sketch, "E71.9.43.0", {"start": v(24.64, 2.03) * mm, "end": v(25.4, 2.03) * mm});
            skLineSegment(sketch, "E71.0.44.0", {"start": v(26.16, 2.8) * mm, "end": v(26.92, 2.8) * mm});
            skLineSegment(sketch, "E71.3.44.0", {"start": v(26.92, 2.8) * mm, "end": v(26.92, 2.03) * mm});
            skLineSegment(sketch, "E71.6.44.0", {"start": v(26.16, 2.8) * mm, "end": v(26.16, 2.03) * mm});
            skLineSegment(sketch, "E71.9.44.0", {"start": v(26.16, 2.03) * mm, "end": v(26.92, 2.03) * mm});
            skLineSegment(sketch, "E71.0.45.0", {"start": v(27.69, 2.8) * mm, "end": v(28.45, 2.8) * mm});
            skLineSegment(sketch, "E71.3.45.0", {"start": v(28.45, 2.8) * mm, "end": v(28.45, 2.03) * mm});
            skLineSegment(sketch, "E71.6.45.0", {"start": v(27.69, 2.8) * mm, "end": v(27.69, 2.03) * mm});
            skLineSegment(sketch, "E71.9.45.0", {"start": v(27.69, 2.03) * mm, "end": v(28.45, 2.03) * mm});
            skLineSegment(sketch, "E71.0.46.0", {"start": v(29.2, 2.8) * mm, "end": v(29.97, 2.8) * mm});
            skLineSegment(sketch, "E71.3.46.0", {"start": v(29.97, 2.8) * mm, "end": v(29.97, 2.03) * mm});
            skLineSegment(sketch, "E71.6.46.0", {"start": v(29.2, 2.8) * mm, "end": v(29.2, 2.03) * mm});
            skLineSegment(sketch, "E71.9.46.0", {"start": v(29.2, 2.03) * mm, "end": v(29.97, 2.03) * mm});
            skLineSegment(sketch, "E71.0.47.0", {"start": v(30.73, 2.8) * mm, "end": v(31.5, 2.8) * mm});
            skLineSegment(sketch, "E71.3.47.0", {"start": v(31.5, 2.8) * mm, "end": v(31.5, 2.03) * mm});
            skLineSegment(sketch, "E71.6.47.0", {"start": v(30.73, 2.8) * mm, "end": v(30.73, 2.03) * mm});
            skLineSegment(sketch, "E71.9.47.0", {"start": v(30.73, 2.03) * mm, "end": v(31.5, 2.03) * mm});
            skLineSegment(sketch, "E71.0.48.0", {"start": v(32.26, 2.8) * mm, "end": v(33.02, 2.8) * mm});
            skLineSegment(sketch, "E71.3.48.0", {"start": v(33.02, 2.8) * mm, "end": v(33.02, 2.03) * mm});
            skLineSegment(sketch, "E71.6.48.0", {"start": v(32.26, 2.8) * mm, "end": v(32.26, 2.03) * mm});
            skLineSegment(sketch, "E71.9.48.0", {"start": v(32.26, 2.03) * mm, "end": v(33.02, 2.03) * mm});
            skLineSegment(sketch, "E71.0.49.0", {"start": v(33.78, 2.8) * mm, "end": v(34.54, 2.8) * mm});
            skLineSegment(sketch, "E71.3.49.0", {"start": v(34.54, 2.8) * mm, "end": v(34.54, 2.03) * mm});
            skLineSegment(sketch, "E71.6.49.0", {"start": v(33.78, 2.8) * mm, "end": v(33.78, 2.03) * mm});
            skLineSegment(sketch, "E71.9.49.0", {"start": v(33.78, 2.03) * mm, "end": v(34.54, 2.03) * mm});
            skLineSegment(sketch, "E72.0.50.0", {"start": v(35.3, 2.8) * mm, "end": v(36.07, 2.8) * mm});
            skLineSegment(sketch, "E72.3.50.0", {"start": v(36.07, 2.8) * mm, "end": v(36.07, 2.03) * mm});
            skLineSegment(sketch, "E72.6.50.0", {"start": v(35.3, 2.8) * mm, "end": v(35.3, 2.03) * mm});
            skLineSegment(sketch, "E72.9.50.0", {"start": v(35.3, 2.03) * mm, "end": v(36.07, 2.03) * mm});
            skLineSegment(sketch, "E72.0.51.0", {"start": v(36.83, 2.8) * mm, "end": v(37.6, 2.8) * mm});
            skLineSegment(sketch, "E72.3.51.0", {"start": v(37.6, 2.8) * mm, "end": v(37.6, 2.03) * mm});
            skLineSegment(sketch, "E72.6.51.0", {"start": v(36.83, 2.8) * mm, "end": v(36.83, 2.03) * mm});
            skLineSegment(sketch, "E72.9.51.0", {"start": v(36.83, 2.03) * mm, "end": v(37.6, 2.03) * mm});
            skLineSegment(sketch, "E72.0.52.0", {"start": v(38.35, 2.8) * mm, "end": v(39.12, 2.8) * mm});
            skLineSegment(sketch, "E72.3.52.0", {"start": v(39.12, 2.8) * mm, "end": v(39.12, 2.03) * mm});
            skLineSegment(sketch, "E72.6.52.0", {"start": v(38.35, 2.8) * mm, "end": v(38.35, 2.03) * mm});
            skLineSegment(sketch, "E72.9.52.0", {"start": v(38.35, 2.03) * mm, "end": v(39.12, 2.03) * mm});
            skLineSegment(sketch, "E72.0.53.0", {"start": v(39.88, 2.8) * mm, "end": v(40.64, 2.8) * mm});
            skLineSegment(sketch, "E72.3.53.0", {"start": v(40.64, 2.8) * mm, "end": v(40.64, 2.03) * mm});
            skLineSegment(sketch, "E72.6.53.0", {"start": v(39.88, 2.8) * mm, "end": v(39.88, 2.03) * mm});
            skLineSegment(sketch, "E72.9.53.0", {"start": v(39.88, 2.03) * mm, "end": v(40.64, 2.03) * mm});
            skSolve(sketch);
        }
        {
            var Q0;
            Q0 = qSketchRegion(id + "F28", true);
            extrude(context, id + "F29", {"entities" : qUnion([Q0]), "operationType" : NewBodyOperationType.REMOVE, "endBound" : BoundingType.UP_TO_NEXT, "oppositeDirection" : true, "depth" : 25.4 * mm});
        }
    });
